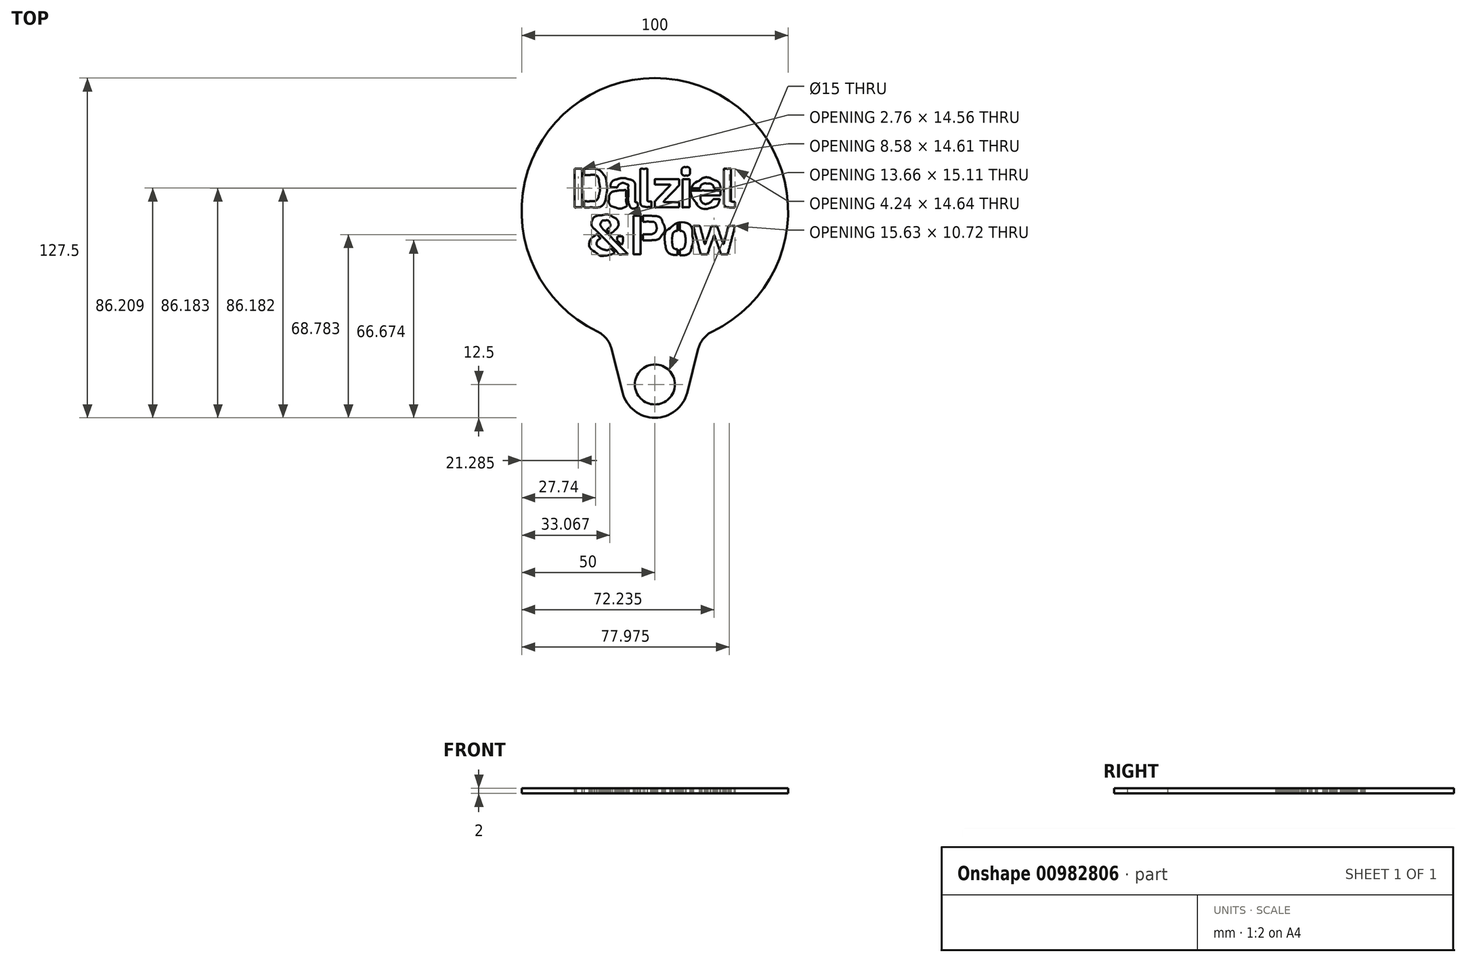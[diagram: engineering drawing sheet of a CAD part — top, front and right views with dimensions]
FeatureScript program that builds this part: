
annotation { "Feature Type Name" : "Feature", "Feature Type Description" : "" }
export const myFeature = defineFeature(function(context is Context, id is Id, definition is map)
    precondition{}
    {
        {
            var Q0;
            Q0=qCreatedBy(makeId("Top.planeOp"),FACE);
            var sketch = newSketch(context, id + "F0", { "sketchPlane" : qUnion([Q0])});
            skArc(sketch, "E0", {"start": v(21.65, -45.07) * mm, "mid": v(0, 50) * mm, "end": v(-21.65, -45.07) * mm});
            skCircle(sketch, "E1", {"center": v(0, -65) * mm, "radius": 7.5 * mm});
            skArc(sketch, "E2", {"start": v(-12.12, -68.07) * mm, "mid": v(0, -77.5) * mm, "end": v(12.12, -68.07) * mm});
            skLineSegment(sketch, "E3", {"start": v(12.12, -68.07) * mm, "end": v(16.29, -51.63) * mm});
            skLineSegment(sketch, "E4", {"start": v(-12.12, -68.07) * mm, "end": v(-16.29, -51.63) * mm});
            skPoint(sketch, "E5.visualSharp", {"position": v(17.5, -46.84) * mm});
            skArc(sketch, "E5.filletArc", {"start": v(21.65, -45.07) * mm, "mid": v(18.24, -47.75) * mm, "end": v(16.29, -51.63) * mm});
            skPoint(sketch, "E6.visualSharp", {"position": v(-17.5, -46.84) * mm});
            skArc(sketch, "E6.filletArc", {"start": v(-16.29, -51.63) * mm, "mid": v(-18.24, -47.75) * mm, "end": v(-21.65, -45.07) * mm});
            skCircle(sketch, "E7", {"center": v(0, 0) * mm, "radius": 40 * mm, "construction": true});
            skSolve(sketch);
        }
        {
            var Q0;
            Q0=makeQuery(id+"F0.imprint","IMPRINT",FACE,{"disambiguationData":[TD([[makeQuery(id+"F0.imprint","IMPRINT",EDGE,{"derivedFrom":sQuery(id+"F0.wireOp",EDGE,"E0")}),1.0]])]});
            extrude(context, id + "F1", {"entities" : qUnion([Q0]), "depth" : 2 * mm, "offsetDistance" : 25 * mm});
        }
        {
            var Q0;
            Q0=makeQuery(id+"F1.opExtrude","CAP_FACE",FACE,{"disambiguationData":[OSD([sQuery(id+"F0.wireOp",EDGE,"E0"),sQuery(id+"F0.wireOp",EDGE,"E1"),sQuery(id+"F0.wireOp",EDGE,"E2"),sQuery(id+"F0.wireOp",EDGE,"E3"),sQuery(id+"F0.wireOp",EDGE,"E4"),sQuery(id+"F0.wireOp",EDGE,"E5.filletArc"),sQuery(id+"F0.wireOp",EDGE,"E6.filletArc")])],"isStart":false});
            var sketch = newSketch(context, id + "F2", { "sketchPlane" : qUnion([Q0])});
            skFitSpline(sketch, "E8", {"points": [v(-115.22, -58.84) * mm, v(-108.7, -64.77) * mm, v(-102.51, -70.4) * mm, v(-95.99, -76.34) * mm]});
            skFitSpline(sketch, "E9", {"points": [v(-95.99, -76.34) * mm, v(-95.26, -72.37) * mm, v(-94.43, -67.86) * mm, v(-93.51, -62.86) * mm]});
            skFitSpline(sketch, "E10", {"points": [v(-93.51, -62.86) * mm, v(-89.6, -62.86) * mm, v(-85.37, -62.77) * mm, v(-81.15, -62.96) * mm, v(-80.64, -62.98) * mm, v(-79.78, -64.47) * mm, v(-79.78, -65.27) * mm]});
            skFitSpline(sketch, "E11", {"points": [v(-79.78, -65.27) * mm, v(-79.84, -72.6) * mm, v(-80.93, -79.77) * mm, v(-84.6, -86.27) * mm]});
            skFitSpline(sketch, "E12", {"points": [v(-84.6, -86.27) * mm, v(-85.64, -88.12) * mm, v(-85.45, -89.2) * mm, v(-84, -90.64) * mm, v(-78.63, -95.97) * mm, v(-73.37, -101.42) * mm, v(-67.36, -107.55) * mm]});
            skFitSpline(sketch, "E13", {"points": [v(-67.36, -107.55) * mm, v(-72.03, -107.55) * mm, v(-75.8, -107.55) * mm, v(-79.58, -107.55) * mm, v(-80.11, -107.55) * mm, v(-80.66, -107.48) * mm, v(-81.18, -107.57) * mm]});
            skFitSpline(sketch, "E14", {"points": [v(-81.18, -107.57) * mm, v(-86.67, -108.51) * mm, v(-90.92, -106.64) * mm, v(-94.07, -102.07) * mm]});
            skFitSpline(sketch, "E15", {"points": [v(-94.07, -102.07) * mm, v(-94.3, -101.73) * mm, v(-94.6, -101.45) * mm, v(-94.93, -101.15) * mm]});
            skFitSpline(sketch, "E16", {"points": [v(-94.93, -101.15) * mm, v(-95.27, -100.86) * mm, v(-95.64, -100.56) * mm, v(-96, -100.21) * mm]});
            skFitSpline(sketch, "E17", {"points": [v(-96, -100.21) * mm, v(-101.66, -104.58) * mm, v(-107.8, -107.75) * mm, v(-114.72, -109.12) * mm]});
            skFitSpline(sketch, "E18", {"points": [v(-114.72, -109.12) * mm, v(-126.83, -111.51) * mm, v(-138.43, -110.51) * mm, v(-148.52, -102.67) * mm, v(-161.86, -92.3) * mm, v(-162.73, -73.3) * mm, v(-150.49, -61.65) * mm]});
            skFitSpline(sketch, "E19", {"points": [v(-150.49, -61.65) * mm, v(-147.66, -58.96) * mm, v(-144.36, -56.75) * mm, v(-141.02, -54.12) * mm]});
            skFitSpline(sketch, "E20", {"points": [v(-141.02, -54.12) * mm, v(-142.36, -52.6) * mm, v(-143.68, -51.12) * mm, v(-145, -49.63) * mm]});
            skFitSpline(sketch, "E21", {"points": [v(-145, -49.63) * mm, v(-158.06, -34.86) * mm, v(-151.72, -14.63) * mm, v(-132.53, -10.05) * mm]});
            skFitSpline(sketch, "E22", {"points": [v(-132.53, -10.05) * mm, v(-123.34, -7.85) * mm, v(-114.4, -8.67) * mm, v(-106.25, -13.71) * mm]});
            skFitSpline(sketch, "E23", {"points": [v(-106.25, -13.71) * mm, v(-94.34, -21.08) * mm, v(-91.86, -37.55) * mm, v(-101.24, -47.98) * mm]});
            skFitSpline(sketch, "E24", {"points": [v(-101.24, -47.98) * mm, v(-104.27, -51.34) * mm, v(-108.26, -53.83) * mm, v(-111.84, -56.67) * mm]});
            skFitSpline(sketch, "E25", {"points": [v(-111.84, -56.67) * mm, v(-112.73, -57.38) * mm, v(-113.75, -57.9) * mm, v(-115.22, -58.84) * mm]});
            skFitSpline(sketch, "E26", {"points": [v(-106.68, -89.79) * mm, v(-107.44, -88.82) * mm, v(-107.9, -88.13) * mm, v(-108.47, -87.54) * mm]});
            skFitSpline(sketch, "E27", {"points": [v(-108.47, -87.54) * mm, v(-114.29, -81.44) * mm, v(-120.12, -75.35) * mm, v(-125.96, -69.28) * mm, v(-130.75, -64.32) * mm, v(-130.76, -64.33) * mm, v(-136.43, -68.46) * mm]});
            skFitSpline(sketch, "E28", {"points": [v(-136.43, -68.46) * mm, v(-143.99, -73.95) * mm, v(-145.29, -83.81) * mm, v(-138.9, -90.1) * mm]});
            skFitSpline(sketch, "E29", {"points": [v(-138.9, -90.1) * mm, v(-136.72, -92.25) * mm, v(-133.7, -94.03) * mm, v(-130.76, -94.81) * mm, v(-122.11, -97.1) * mm, v(-113.96, -95.93) * mm, v(-106.68, -89.79) * mm]});
            skFitSpline(sketch, "E30", {"points": [v(-123.71, -22.65) * mm, v(-128.16, -22.58) * mm, v(-132, -23.9) * mm, v(-134.27, -27.96) * mm]});
            skFitSpline(sketch, "E31", {"points": [v(-134.27, -27.96) * mm, v(-136.7, -32.27) * mm, v(-135.63, -36.43) * mm, v(-133, -40.28) * mm]});
            skFitSpline(sketch, "E32", {"points": [v(-133, -40.28) * mm, v(-130.2, -44.4) * mm, v(-127.93, -46.57) * mm, v(-125.44, -46.93) * mm]});
            skFitSpline(sketch, "E33", {"points": [v(-125.44, -46.93) * mm, v(-122.96, -47.29) * mm, v(-120.24, -45.83) * mm, v(-116.54, -42.67) * mm]});
            skFitSpline(sketch, "E34", {"points": [v(-116.54, -42.67) * mm, v(-112.54, -39.25) * mm, v(-111.09, -34.1) * mm, v(-112.8, -29.39) * mm]});
            skFitSpline(sketch, "E35", {"points": [v(-112.8, -29.39) * mm, v(-114.33, -25.13) * mm, v(-118.23, -22.72) * mm, v(-123.71, -22.65) * mm]});
            skFitSpline(sketch, "E36", {"points": [v(-200.46, 58.06) * mm, v(-200.46, 72.91) * mm, v(-200.4, 87.77) * mm, v(-200.52, 102.63) * mm]});
            skFitSpline(sketch, "E37", {"points": [v(-200.52, 102.63) * mm, v(-200.54, 105.52) * mm, v(-199.8, 106.47) * mm, v(-196.77, 106.43) * mm]});
            skFitSpline(sketch, "E38", {"points": [v(-196.77, 106.43) * mm, v(-184.27, 106.25) * mm, v(-171.75, 106.6) * mm, v(-159.26, 106.27) * mm]});
            skFitSpline(sketch, "E39", {"points": [v(-159.26, 106.27) * mm, v(-148.14, 105.98) * mm, v(-137.97, 102.84) * mm, v(-130.22, 94.2) * mm, v(-124.58, 87.92) * mm, v(-121.83, 80.37) * mm, v(-120.81, 72.16) * mm, v(-120.11, 66.51) * mm, v(-119.74, 60.86) * mm, v(-119.86, 55.22) * mm]});
            skFitSpline(sketch, "E40", {"points": [v(-119.86, 55.22) * mm, v(-119.98, 49.59) * mm, v(-120.6, 43.97) * mm, v(-121.87, 38.38) * mm]});
            skFitSpline(sketch, "E41", {"points": [v(-121.87, 38.38) * mm, v(-125.76, 21.35) * mm, v(-139.23, 10.19) * mm, v(-156.73, 9.85) * mm]});
            skFitSpline(sketch, "E42", {"points": [v(-156.73, 9.85) * mm, v(-170.3, 9.58) * mm, v(-183.87, 9.81) * mm, v(-197.45, 9.68) * mm]});
            skFitSpline(sketch, "E43", {"points": [v(-197.45, 9.68) * mm, v(-199.94, 9.65) * mm, v(-200.48, 10.57) * mm, v(-200.47, 12.85) * mm]});
            skFitSpline(sketch, "E44", {"points": [v(-200.47, 12.85) * mm, v(-200.4, 27.92) * mm, v(-200.43, 42.99) * mm, v(-200.43, 58.06) * mm]});
            skFitSpline(sketch, "E45", {"points": [v(-200.43, 58.06) * mm, v(-200.44, 58.06) * mm, v(-200.45, 58.06) * mm, v(-200.46, 58.06) * mm]});
            skFitSpline(sketch, "E46", {"points": [v(-182.32, 57.9) * mm, v(-182.32, 52.99) * mm, v(-182.32, 48.08) * mm, v(-182.32, 43.16) * mm, v(-182.32, 38.14) * mm, v(-182.3, 33.12) * mm, v(-182.35, 28.1) * mm]});
            skFitSpline(sketch, "E47", {"points": [v(-182.35, 28.1) * mm, v(-182.36, 26.32) * mm, v(-182.2, 24.93) * mm, v(-179.85, 24.96) * mm]});
            skFitSpline(sketch, "E48", {"points": [v(-179.85, 24.96) * mm, v(-172.91, 25.05) * mm, v(-165.95, 24.77) * mm, v(-159.03, 25.15) * mm, v(-149.46, 25.67) * mm, v(-142.81, 31.1) * mm, v(-140.32, 40.4) * mm]});
            skFitSpline(sketch, "E49", {"points": [v(-140.32, 40.4) * mm, v(-137.48, 50.97) * mm, v(-137.51, 61.79) * mm, v(-139.6, 72.44) * mm]});
            skFitSpline(sketch, "E50", {"points": [v(-139.6, 72.44) * mm, v(-142.12, 85.3) * mm, v(-149.21, 90.75) * mm, v(-162.25, 90.81) * mm]});
            skFitSpline(sketch, "E51", {"points": [v(-162.25, 90.81) * mm, v(-167.8, 90.84) * mm, v(-173.36, 90.7) * mm, v(-178.91, 90.87) * mm]});
            skFitSpline(sketch, "E52", {"points": [v(-178.91, 90.87) * mm, v(-181.6, 90.95) * mm, v(-182.4, 90.02) * mm, v(-182.37, 87.4) * mm, v(-182.25, 77.56) * mm, v(-182.32, 67.73) * mm, v(-182.32, 57.9) * mm]});
            skFitSpline(sketch, "E53", {"points": [v(96.27, -36.8) * mm, v(101.4, -36.8) * mm, v(106.4, -36.7) * mm, v(111.4, -36.9) * mm]});
            skFitSpline(sketch, "E54", {"points": [v(111.4, -36.9) * mm, v(112.1, -36.94) * mm, v(113.14, -38.32) * mm, v(113.39, -39.24) * mm]});
            skFitSpline(sketch, "E55", {"points": [v(113.39, -39.24) * mm, v(116.9, -52.55) * mm, v(120.32, -65.88) * mm, v(123.77, -79.2) * mm]});
            skFitSpline(sketch, "E56", {"points": [v(123.77, -79.2) * mm, v(124.05, -80.3) * mm, v(124.38, -81.4) * mm, v(125.38, -82.6) * mm]});
            skFitSpline(sketch, "E57", {"points": [v(125.38, -82.6) * mm, v(125.89, -81.4) * mm, v(126.48, -80.23) * mm, v(126.9, -79) * mm]});
            skFitSpline(sketch, "E58", {"points": [v(126.9, -79) * mm, v(131.27, -66.29) * mm, v(135.68, -53.59) * mm, v(139.9, -40.83) * mm]});
            skFitSpline(sketch, "E59", {"points": [v(139.9, -40.83) * mm, v(140.7, -38.4) * mm, v(141.77, -37.31) * mm, v(144.4, -37.5) * mm]});
            skFitSpline(sketch, "E60", {"points": [v(144.4, -37.5) * mm, v(147.26, -37.72) * mm, v(150.16, -37.65) * mm, v(153.04, -37.54) * mm]});
            skFitSpline(sketch, "E61", {"points": [v(153.04, -37.54) * mm, v(155.08, -37.45) * mm, v(156.02, -38.24) * mm, v(156.7, -40.2) * mm]});
            skFitSpline(sketch, "E62", {"points": [v(156.7, -40.2) * mm, v(161.05, -53.04) * mm, v(165.54, -65.82) * mm, v(170, -78.62) * mm, v(170.45, -79.9) * mm, v(170.96, -81.16) * mm, v(171.44, -82.43) * mm]});
            skFitSpline(sketch, "E63", {"points": [v(171.44, -82.43) * mm, v(171.73, -82.45) * mm, v(172.01, -82.46) * mm, v(172.3, -82.48) * mm]});
            skFitSpline(sketch, "E64", {"points": [v(172.3, -82.48) * mm, v(173.31, -78.46) * mm, v(174.33, -74.44) * mm, v(175.34, -70.4) * mm]});
            skFitSpline(sketch, "E65", {"points": [v(175.34, -70.4) * mm, v(177.88, -60.27) * mm, v(180.46, -50.14) * mm, v(182.9, -39.97) * mm]});
            skFitSpline(sketch, "E66", {"points": [v(182.9, -39.97) * mm, v(183.47, -37.64) * mm, v(184.4, -36.56) * mm, v(187, -36.7) * mm]});
            skFitSpline(sketch, "E67", {"points": [v(187, -36.7) * mm, v(191.24, -36.92) * mm, v(195.5, -36.76) * mm, v(200.35, -36.76) * mm]});
            skFitSpline(sketch, "E68", {"points": [v(200.35, -36.76) * mm, v(199.1, -41.88) * mm, v(198, -46.6) * mm, v(196.78, -51.28) * mm]});
            skFitSpline(sketch, "E69", {"points": [v(196.78, -51.28) * mm, v(192.2, -68.93) * mm, v(187.55, -86.57) * mm, v(183.05, -104.25) * mm]});
            skFitSpline(sketch, "E70", {"points": [v(183.05, -104.25) * mm, v(182.4, -106.76) * mm, v(181.37, -107.8) * mm, v(178.7, -107.6) * mm]});
            skFitSpline(sketch, "E71", {"points": [v(178.7, -107.6) * mm, v(175.52, -107.37) * mm, v(172.29, -107.4) * mm, v(169.1, -107.6) * mm]});
            skFitSpline(sketch, "E72", {"points": [v(169.1, -107.6) * mm, v(166.55, -107.76) * mm, v(165.31, -106.9) * mm, v(164.46, -104.42) * mm]});
            skFitSpline(sketch, "E73", {"points": [v(164.46, -104.42) * mm, v(159.8, -90.9) * mm, v(154.94, -77.46) * mm, v(150.14, -63.99) * mm]});
            skFitSpline(sketch, "E74", {"points": [v(150.14, -63.99) * mm, v(149.72, -62.8) * mm, v(149.2, -61.65) * mm, v(148.36, -59.55) * mm]});
            skFitSpline(sketch, "E75", {"points": [v(148.36, -59.55) * mm, v(147.61, -61.4) * mm, v(147.17, -62.38) * mm, v(146.82, -63.4) * mm, v(142, -77.09) * mm, v(137.16, -90.77) * mm, v(132.46, -104.5) * mm]});
            skFitSpline(sketch, "E76", {"points": [v(132.46, -104.5) * mm, v(131.67, -106.77) * mm, v(130.6, -107.74) * mm, v(128.13, -107.6) * mm]});
            skFitSpline(sketch, "E77", {"points": [v(128.13, -107.6) * mm, v(124.5, -107.39) * mm, v(120.85, -107.7) * mm, v(117.24, -107.44) * mm, v(116.19, -107.37) * mm, v(114.57, -106.31) * mm, v(114.32, -105.4) * mm]});
            skFitSpline(sketch, "E78", {"points": [v(114.32, -105.4) * mm, v(108.17, -82.97) * mm, v(102.18, -60.5) * mm, v(96.17, -38.03) * mm]});
            skFitSpline(sketch, "E79", {"points": [v(96.17, -38.03) * mm, v(96.12, -37.85) * mm, v(96.2, -37.62) * mm, v(96.27, -36.8) * mm]});
            skFitSpline(sketch, "E80", {"points": [v(-53.69, -10.92) * mm, v(-51.83, -10.92) * mm, v(-50.46, -10.9) * mm, v(-49.1, -10.92) * mm]});
            skFitSpline(sketch, "E81", {"points": [v(-49.1, -10.92) * mm, v(-34.57, -11.11) * mm, v(-20.01, -10.76) * mm, v(-5.54, -11.68) * mm]});
            skFitSpline(sketch, "E82", {"points": [v(-5.54, -11.68) * mm, v(5.55, -12.4) * mm, v(15.07, -17.37) * mm, v(19.71, -28.18) * mm]});
            skFitSpline(sketch, "E83", {"points": [v(19.71, -28.18) * mm, v(24.46, -39.24) * mm, v(24.01, -50.38) * mm, v(16.78, -60.45) * mm]});
            skFitSpline(sketch, "E84", {"points": [v(16.78, -60.45) * mm, v(10.77, -68.83) * mm, v(1.72, -71.82) * mm, v(-8.05, -72.47) * mm, v(-16.04, -73) * mm, v(-24.07, -72.8) * mm, v(-32.09, -72.72) * mm]});
            skFitSpline(sketch, "E85", {"points": [v(-32.09, -72.72) * mm, v(-33.4, -72.7) * mm, v(-34.29, -72.92) * mm, v(-34.83, -73.46) * mm]});
            skFitSpline(sketch, "E86", {"points": [v(-34.83, -73.46) * mm, v(-35.37, -74) * mm, v(-35.59, -74.89) * mm, v(-35.57, -76.21) * mm, v(-35.45, -85.5) * mm, v(-35.6, -94.8) * mm, v(-35.5, -104.1) * mm]});
            skFitSpline(sketch, "E87", {"points": [v(-35.5, -104.1) * mm, v(-35.46, -106.7) * mm, v(-36.17, -107.78) * mm, v(-38.9, -107.64) * mm]});
            skFitSpline(sketch, "E88", {"points": [v(-38.9, -107.64) * mm, v(-42.64, -107.46) * mm, v(-46.4, -107.45) * mm, v(-50.12, -107.66) * mm]});
            skFitSpline(sketch, "E89", {"points": [v(-50.12, -107.66) * mm, v(-52.89, -107.8) * mm, v(-53.76, -106.96) * mm, v(-53.75, -104.08) * mm]});
            skFitSpline(sketch, "E90", {"points": [v(-53.75, -104.08) * mm, v(-53.64, -75.76) * mm, v(-53.69, -47.44) * mm, v(-53.69, -19.13) * mm]});
            skFitSpline(sketch, "E91", {"points": [v(-53.69, -19.13) * mm, v(-53.69, -16.58) * mm, v(-53.69, -14.02) * mm, v(-53.69, -10.92) * mm]});
            skFitSpline(sketch, "E92", {"points": [v(-35.52, -42.1) * mm, v(-35.52, -46.38) * mm, v(-35.46, -50.65) * mm, v(-35.55, -54.91) * mm]});
            skFitSpline(sketch, "E93", {"points": [v(-35.55, -54.91) * mm, v(-35.59, -56.86) * mm, v(-35.12, -57.82) * mm, v(-32.89, -57.79) * mm]});
            skFitSpline(sketch, "E94", {"points": [v(-32.89, -57.79) * mm, v(-25.74, -57.66) * mm, v(-18.58, -57.98) * mm, v(-11.45, -57.59) * mm]});
            skFitSpline(sketch, "E95", {"points": [v(-11.45, -57.59) * mm, v(-8.38, -57.42) * mm, v(-5.1, -56.41) * mm, v(-2.4, -54.9) * mm]});
            skFitSpline(sketch, "E96", {"points": [v(-2.4, -54.9) * mm, v(0.32, -53.37) * mm, v(2.26, -50.86) * mm, v(3.33, -47.89) * mm]});
            skFitSpline(sketch, "E97", {"points": [v(3.33, -47.89) * mm, v(4.4, -44.91) * mm, v(4.6, -41.47) * mm, v(3.85, -38.06) * mm]});
            skFitSpline(sketch, "E98", {"points": [v(3.85, -38.06) * mm, v(2.4, -31.54) * mm, v(-2.28, -26.93) * mm, v(-9.32, -26.42) * mm]});
            skFitSpline(sketch, "E99", {"points": [v(-9.32, -26.42) * mm, v(-17.28, -25.83) * mm, v(-25.3, -26.07) * mm, v(-33.3, -25.93) * mm]});
            skFitSpline(sketch, "E100", {"points": [v(-33.3, -25.93) * mm, v(-35.26, -25.9) * mm, v(-35.53, -27.11) * mm, v(-35.52, -28.66) * mm, v(-35.5, -33.15) * mm, v(-35.51, -37.63) * mm, v(-35.52, -42.1) * mm]});
            skFitSpline(sketch, "E101", {"points": [v(-110.6, 59.65) * mm, v(-110.02, 69.52) * mm, v(-103.97, 77.04) * mm, v(-94.11, 80.03) * mm]});
            skFitSpline(sketch, "E102", {"points": [v(-94.11, 80.03) * mm, v(-84.93, 82.8) * mm, v(-75.58, 83) * mm, v(-66.32, 80.33) * mm]});
            skFitSpline(sketch, "E103", {"points": [v(-66.32, 80.33) * mm, v(-55.87, 77.32) * mm, v(-49.85, 69.6) * mm, v(-49.6, 58.68) * mm]});
            skFitSpline(sketch, "E104", {"points": [v(-49.6, 58.68) * mm, v(-49.38, 48.96) * mm, v(-49.5, 39.23) * mm, v(-49.47, 29.51) * mm]});
            skFitSpline(sketch, "E105", {"points": [v(-49.47, 29.51) * mm, v(-49.46, 23.34) * mm, v(-49.14, 22.94) * mm, v(-42.98, 22.06) * mm]});
            skFitSpline(sketch, "E106", {"points": [v(-42.98, 22.06) * mm, v(-42.98, 18.63) * mm, v(-42.84, 15.13) * mm, v(-43.09, 11.66) * mm]});
            skFitSpline(sketch, "E107", {"points": [v(-43.09, 11.66) * mm, v(-43.14, 10.88) * mm, v(-44.42, 9.84) * mm, v(-45.35, 9.51) * mm]});
            skFitSpline(sketch, "E108", {"points": [v(-45.35, 9.51) * mm, v(-53.8, 6.5) * mm, v(-60.49, 9.4) * mm, v(-64.11, 16.97) * mm]});
            skFitSpline(sketch, "E109", {"points": [v(-64.11, 16.97) * mm, v(-68.43, 14.49) * mm, v(-72.56, 11.4) * mm, v(-77.2, 9.6) * mm]});
            skFitSpline(sketch, "E110", {"points": [v(-77.2, 9.6) * mm, v(-84.72, 6.7) * mm, v(-92.56, 7.34) * mm, v(-100.1, 10.05) * mm]});
            skFitSpline(sketch, "E111", {"points": [v(-100.1, 10.05) * mm, v(-109.53, 13.43) * mm, v(-114.73, 21.45) * mm, v(-114.28, 31.37) * mm]});
            skFitSpline(sketch, "E112", {"points": [v(-114.28, 31.37) * mm, v(-113.85, 40.67) * mm, v(-107.4, 48.27) * mm, v(-96.96, 50.57) * mm]});
            skFitSpline(sketch, "E113", {"points": [v(-96.96, 50.57) * mm, v(-90.85, 51.91) * mm, v(-84.49, 52.07) * mm, v(-78.23, 52.7) * mm]});
            skFitSpline(sketch, "E114", {"points": [v(-78.23, 52.7) * mm, v(-75.15, 53) * mm, v(-72.06, 53.24) * mm, v(-68.97, 53.38) * mm]});
            skFitSpline(sketch, "E115", {"points": [v(-68.97, 53.38) * mm, v(-67.2, 53.45) * mm, v(-66.6, 54.2) * mm, v(-66.59, 55.95) * mm]});
            skFitSpline(sketch, "E116", {"points": [v(-66.59, 55.95) * mm, v(-66.56, 60.87) * mm, v(-66.49, 65.9) * mm, v(-71.96, 68.22) * mm]});
            skFitSpline(sketch, "E117", {"points": [v(-71.96, 68.22) * mm, v(-77.43, 70.54) * mm, v(-83.14, 70.5) * mm, v(-88.34, 67.62) * mm]});
            skFitSpline(sketch, "E118", {"points": [v(-88.34, 67.62) * mm, v(-90.37, 66.5) * mm, v(-91.88, 64.07) * mm, v(-93.08, 61.93) * mm]});
            skFitSpline(sketch, "E119", {"points": [v(-93.08, 61.93) * mm, v(-93.9, 60.47) * mm, v(-94.46, 59.57) * mm, v(-96.29, 59.61) * mm]});
            skFitSpline(sketch, "E120", {"points": [v(-96.29, 59.61) * mm, v(-101.05, 59.72) * mm, v(-105.81, 59.65) * mm, v(-110.6, 59.65) * mm]});
            skFitSpline(sketch, "E121", {"points": [v(-66.65, 35.75) * mm, v(-66.53, 41.33) * mm, v(-66.53, 41.3) * mm, v(-70.84, 40.92) * mm, v(-72.64, 40.76) * mm, v(-74.47, 40.86) * mm, v(-76.27, 40.64) * mm]});
            skFitSpline(sketch, "E122", {"points": [v(-76.27, 40.64) * mm, v(-81.2, 40.05) * mm, v(-86.24, 39.77) * mm, v(-91.04, 38.56) * mm, v(-93.06, 38.05) * mm, v(-94.63, 36.85) * mm, v(-95.69, 35.33) * mm]});
            skFitSpline(sketch, "E123", {"points": [v(-95.69, 35.33) * mm, v(-96.74, 33.8) * mm, v(-97.28, 31.96) * mm, v(-97.23, 30.17) * mm]});
            skFitSpline(sketch, "E124", {"points": [v(-97.23, 30.17) * mm, v(-97.12, 26.44) * mm, v(-94.43, 23.13) * mm, v(-90.36, 21.86) * mm]});
            skFitSpline(sketch, "E125", {"points": [v(-90.36, 21.86) * mm, v(-85.42, 20.32) * mm, v(-80.62, 21.24) * mm, v(-76.04, 23.16) * mm]});
            skFitSpline(sketch, "E126", {"points": [v(-76.04, 23.16) * mm, v(-69.94, 25.72) * mm, v(-66.94, 30.56) * mm, v(-66.65, 35.75) * mm]});
            skFitSpline(sketch, "E127", {"points": [v(164.3, 40) * mm, v(159.84, 40) * mm, v(156, 40) * mm, v(152.18, 40) * mm]});
            skFitSpline(sketch, "E128", {"points": [v(152.18, 40) * mm, v(140.53, 40) * mm, v(128.88, 40.01) * mm, v(117.23, 40) * mm]});
            skFitSpline(sketch, "E129", {"points": [v(117.23, 40) * mm, v(113.68, 40) * mm, v(113.33, 39.56) * mm, v(113.92, 36.1) * mm]});
            skFitSpline(sketch, "E130", {"points": [v(113.92, 36.1) * mm, v(115.91, 24.55) * mm, v(126.74, 17.96) * mm, v(137.66, 22.16) * mm]});
            skFitSpline(sketch, "E131", {"points": [v(137.66, 22.16) * mm, v(140.39, 23.2) * mm, v(142.36, 26.2) * mm, v(144.69, 28.28) * mm, v(145.49, 29) * mm, v(146.3, 30.23) * mm, v(147.14, 30.26) * mm]});
            skFitSpline(sketch, "E132", {"points": [v(147.14, 30.26) * mm, v(152.03, 30.45) * mm, v(156.93, 30.35) * mm, v(162.33, 30.35) * mm]});
            skFitSpline(sketch, "E133", {"points": [v(162.33, 30.35) * mm, v(161.97, 28.75) * mm, v(161.84, 27.52) * mm, v(161.4, 26.42) * mm]});
            skFitSpline(sketch, "E134", {"points": [v(161.4, 26.42) * mm, v(157.5, 16.56) * mm, v(150.09, 11) * mm, v(139.86, 8.75) * mm]});
            skFitSpline(sketch, "E135", {"points": [v(139.86, 8.75) * mm, v(124.59, 5.4) * mm, v(110.22, 10.65) * mm, v(102, 22.75) * mm, v(90.89, 39.14) * mm, v(94.82, 65.68) * mm, v(110.38, 76.16) * mm]});
            skFitSpline(sketch, "E136", {"points": [v(110.38, 76.16) * mm, v(121.95, 83.95) * mm, v(134.65, 84.3) * mm, v(147, 78.37) * mm]});
            skFitSpline(sketch, "E137", {"points": [v(147, 78.37) * mm, v(158.8, 72.7) * mm, v(163.78, 62.2) * mm, v(164.28, 49.42) * mm]});
            skFitSpline(sketch, "E138", {"points": [v(164.28, 49.42) * mm, v(164.4, 46.46) * mm, v(164.3, 43.48) * mm, v(164.3, 40) * mm]});
            skFitSpline(sketch, "E139", {"points": [v(146.4, 51.95) * mm, v(146.81, 61.72) * mm, v(141.05, 68.35) * mm, v(132.19, 68.91) * mm]});
            skFitSpline(sketch, "E140", {"points": [v(132.19, 68.91) * mm, v(122.38, 69.53) * mm, v(114.57, 63.44) * mm, v(113.7, 54.59) * mm]});
            skFitSpline(sketch, "E141", {"points": [v(113.7, 54.59) * mm, v(113.6, 53.6) * mm, v(113.71, 52.93) * mm, v(114.1, 52.5) * mm]});
            skFitSpline(sketch, "E142", {"points": [v(114.1, 52.5) * mm, v(114.49, 52.08) * mm, v(115.15, 51.9) * mm, v(116.14, 51.93) * mm]});
            skFitSpline(sketch, "E143", {"points": [v(116.14, 51.93) * mm, v(120.2, 52.02) * mm, v(124.26, 51.95) * mm, v(128.33, 51.95) * mm]});
            skFitSpline(sketch, "E144", {"points": [v(128.33, 51.95) * mm, v(134.29, 51.95) * mm, v(140.25, 51.95) * mm, v(146.4, 51.95) * mm]});
            skFitSpline(sketch, "E145", {"points": [v(24.46, -72.26) * mm, v(24.69, -60.05) * mm, v(28.1, -49.32) * mm, v(38.3, -41.88) * mm, v(56.4, -28.65) * mm, v(88.12, -34.4) * mm, v(93.87, -62) * mm]});
            skFitSpline(sketch, "E146", {"points": [v(93.87, -62) * mm, v(95.66, -70.6) * mm, v(95.46, -79.22) * mm, v(92.44, -87.56) * mm]});
            skFitSpline(sketch, "E147", {"points": [v(92.44, -87.56) * mm, v(86.2, -104.83) * mm, v(70.04, -110.5) * mm, v(56.63, -109.31) * mm]});
            skFitSpline(sketch, "E148", {"points": [v(56.63, -109.31) * mm, v(40.96, -107.93) * mm, v(30, -98.87) * mm, v(26.25, -84.56) * mm]});
            skFitSpline(sketch, "E149", {"points": [v(26.25, -84.56) * mm, v(25.2, -80.58) * mm, v(25.03, -76.36) * mm, v(24.46, -72.26) * mm]});
            skFitSpline(sketch, "E150", {"points": [v(42.57, -72.15) * mm, v(42.91, -75.25) * mm, v(43.03, -78.47) * mm, v(43.66, -81.59) * mm]});
            skFitSpline(sketch, "E151", {"points": [v(43.66, -81.59) * mm, v(45.28, -89.66) * mm, v(51.4, -94.77) * mm, v(59.36, -95.02) * mm]});
            skFitSpline(sketch, "E152", {"points": [v(59.36, -95.02) * mm, v(67.24, -95.27) * mm, v(73.69, -90.4) * mm, v(75.73, -82.44) * mm]});
            skFitSpline(sketch, "E153", {"points": [v(75.73, -82.44) * mm, v(76.57, -79.18) * mm, v(77, -75.9) * mm, v(77.03, -72.63) * mm]});
            skFitSpline(sketch, "E154", {"points": [v(77.03, -72.63) * mm, v(77.06, -69.35) * mm, v(76.68, -66.07) * mm, v(75.89, -62.8) * mm]});
            skFitSpline(sketch, "E155", {"points": [v(75.89, -62.8) * mm, v(73.82, -54.27) * mm, v(67.61, -49.31) * mm, v(59.44, -49.5) * mm]});
            skFitSpline(sketch, "E156", {"points": [v(59.44, -49.5) * mm, v(51.22, -49.68) * mm, v(45.2, -54.9) * mm, v(43.59, -63.48) * mm, v(43.06, -66.3) * mm, v(42.9, -69.18) * mm, v(42.57, -72.15) * mm]});
            skFitSpline(sketch, "E157", {"points": [v(38.72, 66.86) * mm, v(37.5, 66.86) * mm, v(36.26, 66.86) * mm, v(35.03, 66.86) * mm]});
            skFitSpline(sketch, "E158", {"points": [v(35.03, 66.86) * mm, v(24.67, 66.85) * mm, v(14.3, 67) * mm, v(3.94, 66.77) * mm]});
            skFitSpline(sketch, "E159", {"points": [v(3.94, 66.77) * mm, v(0.54, 66.69) * mm, v(-0.36, 67.84) * mm, v(-0.06, 70.95) * mm]});
            skFitSpline(sketch, "E160", {"points": [v(-0.06, 70.95) * mm, v(0.16, 73.17) * mm, v(0.06, 75.44) * mm, v(-0.03, 77.68) * mm]});
            skFitSpline(sketch, "E161", {"points": [v(-0.03, 77.68) * mm, v(-0.11, 79.57) * mm, v(0.56, 80.32) * mm, v(2.54, 80.32) * mm, v(20.92, 80.26) * mm, v(39.3, 80.26) * mm, v(57.67, 80.32) * mm]});
            skFitSpline(sketch, "E162", {"points": [v(57.67, 80.32) * mm, v(59.8, 80.33) * mm, v(60.35, 79.53) * mm, v(60.42, 77.51) * mm]});
            skFitSpline(sketch, "E163", {"points": [v(60.42, 77.51) * mm, v(60.85, 65.66) * mm, v(60.91, 65.65) * mm, v(52.76, 57.02) * mm]});
            skFitSpline(sketch, "E164", {"points": [v(52.76, 57.02) * mm, v(43.15, 46.85) * mm, v(33.5, 36.71) * mm, v(23.87, 26.56) * mm, v(23.08, 25.72) * mm, v(22.32, 24.86) * mm, v(21.74, 23.16) * mm]});
            skFitSpline(sketch, "E165", {"points": [v(21.74, 23.16) * mm, v(28.16, 23.16) * mm, v(34.59, 23.16) * mm, v(41.01, 23.16) * mm, v(47.5, 23.16) * mm, v(54, 23.16) * mm, v(60.68, 23.16) * mm]});
            skFitSpline(sketch, "E166", {"points": [v(60.68, 23.16) * mm, v(60.68, 18.65) * mm, v(60.68, 14.52) * mm, v(60.68, 10) * mm]});
            skFitSpline(sketch, "E167", {"points": [v(60.68, 10) * mm, v(59.73, 9.91) * mm, v(58.72, 9.75) * mm, v(57.7, 9.75) * mm, v(39.54, 9.73) * mm, v(21.38, 9.78) * mm, v(3.22, 9.68) * mm]});
            skFitSpline(sketch, "E168", {"points": [v(3.22, 9.68) * mm, v(0.52, 9.67) * mm, v(-0.22, 10.58) * mm, v(-0.26, 13.17) * mm, v(-0.43, 24.02) * mm, v(-0.53, 24.04) * mm, v(6.92, 31.95) * mm]});
            skFitSpline(sketch, "E169", {"points": [v(6.92, 31.95) * mm, v(16.82, 42.44) * mm, v(26.76, 52.88) * mm, v(36.68, 63.35) * mm]});
            skFitSpline(sketch, "E170", {"points": [v(36.68, 63.35) * mm, v(37.48, 64.2) * mm, v(38.24, 65.06) * mm, v(39.01, 65.92) * mm]});
            skFitSpline(sketch, "E171", {"points": [v(39.01, 65.92) * mm, v(38.92, 66.23) * mm, v(38.82, 66.54) * mm, v(38.72, 66.86) * mm]});
            skFitSpline(sketch, "E172", {"points": [v(200.5, 23.13) * mm, v(200.5, 19.12) * mm, v(200.64, 15.28) * mm, v(200.38, 11.47) * mm]});
            skFitSpline(sketch, "E173", {"points": [v(200.38, 11.47) * mm, v(200.32, 10.66) * mm, v(198.8, 9.31) * mm, v(197.96, 9.31) * mm]});
            skFitSpline(sketch, "E174", {"points": [v(197.96, 9.31) * mm, v(193.4, 9.32) * mm, v(188.71, 9.1) * mm, v(184.3, 10.05) * mm]});
            skFitSpline(sketch, "E175", {"points": [v(184.3, 10.05) * mm, v(177.06, 11.62) * mm, v(172.73, 17.72) * mm, v(172.63, 25.7) * mm]});
            skFitSpline(sketch, "E176", {"points": [v(172.63, 25.7) * mm, v(172.48, 37.77) * mm, v(172.56, 49.84) * mm, v(172.55, 61.9) * mm]});
            skFitSpline(sketch, "E177", {"points": [v(172.55, 61.9) * mm, v(172.55, 68.74) * mm, v(172.56, 75.57) * mm, v(172.56, 82.4) * mm]});
            skFitSpline(sketch, "E178", {"points": [v(172.56, 82.4) * mm, v(172.57, 89.24) * mm, v(172.56, 96.08) * mm, v(172.5, 102.91) * mm]});
            skFitSpline(sketch, "E179", {"points": [v(172.5, 102.91) * mm, v(172.49, 105.52) * mm, v(173.22, 106.55) * mm, v(175.93, 106.4) * mm]});
            skFitSpline(sketch, "E180", {"points": [v(175.93, 106.4) * mm, v(179.55, 106.2) * mm, v(183.2, 106.18) * mm, v(186.82, 106.4) * mm]});
            skFitSpline(sketch, "E181", {"points": [v(186.82, 106.4) * mm, v(189.7, 106.59) * mm, v(190.4, 105.5) * mm, v(190.39, 102.74) * mm]});
            skFitSpline(sketch, "E182", {"points": [v(190.39, 102.74) * mm, v(190.28, 80) * mm, v(190.32, 57.25) * mm, v(190.33, 34.5) * mm]});
            skFitSpline(sketch, "E183", {"points": [v(190.33, 34.5) * mm, v(190.33, 24.4) * mm, v(190.34, 24.4) * mm, v(200.5, 23.13) * mm]});
            skFitSpline(sketch, "E184", {"points": [v(-8.46, 24.27) * mm, v(-8.46, 20.28) * mm, v(-8.36, 16.34) * mm, v(-8.56, 12.42) * mm]});
            skFitSpline(sketch, "E185", {"points": [v(-8.56, 12.42) * mm, v(-8.6, 11.76) * mm, v(-9.9, 10.61) * mm, v(-10.61, 10.62) * mm]});
            skFitSpline(sketch, "E186", {"points": [v(-10.61, 10.62) * mm, v(-15.48, 10.7) * mm, v(-20.48, 10.41) * mm, v(-25.18, 11.42) * mm]});
            skFitSpline(sketch, "E187", {"points": [v(-25.18, 11.42) * mm, v(-31.58, 12.8) * mm, v(-35.85, 18.55) * mm, v(-36.35, 25.15) * mm, v(-36.63, 28.87) * mm, v(-36.6, 32.62) * mm, v(-36.6, 36.36) * mm, v(-36.63, 58.38) * mm, v(-36.56, 80.4) * mm, v(-36.68, 102.42) * mm]});
            skFitSpline(sketch, "E188", {"points": [v(-36.68, 102.42) * mm, v(-36.68, 103.94) * mm, v(-36.49, 105) * mm, v(-35.9, 105.64) * mm]});
            skFitSpline(sketch, "E189", {"points": [v(-35.9, 105.64) * mm, v(-35.3, 106.3) * mm, v(-34.32, 106.53) * mm, v(-32.74, 106.41) * mm, v(-29.34, 106.16) * mm, v(-25.89, 106.16) * mm, v(-22.48, 106.41) * mm, v(-19.6, 106.62) * mm, v(-18.85, 105.54) * mm, v(-18.86, 102.78) * mm]});
            skFitSpline(sketch, "E190", {"points": [v(-18.86, 102.78) * mm, v(-18.96, 85.25) * mm, v(-18.92, 67.72) * mm, v(-18.92, 50.2) * mm]});
            skFitSpline(sketch, "E191", {"points": [v(-18.92, 50.2) * mm, v(-18.92, 44.63) * mm, v(-18.95, 39.08) * mm, v(-18.9, 33.52) * mm, v(-18.85, 26.39) * mm, v(-17.64, 25.13) * mm, v(-10.63, 24.65) * mm]});
            skFitSpline(sketch, "E192", {"points": [v(-10.63, 24.65) * mm, v(-10, 24.6) * mm, v(-9.4, 24.44) * mm, v(-8.46, 24.27) * mm]});
            skFitSpline(sketch, "E193", {"points": [v(86.73, 9.74) * mm, v(81.2, 9.74) * mm, v(76.18, 9.8) * mm, v(71.17, 9.72) * mm]});
            skFitSpline(sketch, "E194", {"points": [v(71.17, 9.72) * mm, v(68.9, 9.68) * mm, v(68.92, 11.1) * mm, v(68.92, 12.68) * mm]});
            skFitSpline(sketch, "E195", {"points": [v(68.92, 12.68) * mm, v(68.93, 22.09) * mm, v(68.91, 31.5) * mm, v(68.91, 40.9) * mm]});
            skFitSpline(sketch, "E196", {"points": [v(68.91, 40.9) * mm, v(68.91, 46.78) * mm, v(68.91, 52.66) * mm, v(68.91, 58.54) * mm]});
            skFitSpline(sketch, "E197", {"points": [v(68.91, 58.54) * mm, v(68.91, 64.42) * mm, v(68.92, 70.3) * mm, v(68.93, 76.18) * mm]});
            skFitSpline(sketch, "E198", {"points": [v(68.93, 76.18) * mm, v(68.93, 77.44) * mm, v(69.07, 78.69) * mm, v(69.15, 80.1) * mm]});
            skFitSpline(sketch, "E199", {"points": [v(69.15, 80.1) * mm, v(75.15, 80.1) * mm, v(80.87, 80.1) * mm, v(86.73, 80.1) * mm]});
            skFitSpline(sketch, "E200", {"points": [v(86.73, 80.1) * mm, v(86.73, 56.65) * mm, v(86.73, 33.4) * mm, v(86.73, 9.74) * mm]});
            skFitSpline(sketch, "E201", {"points": [v(87.87, 100) * mm, v(87.9, 94.13) * mm, v(83.5, 89.6) * mm, v(77.68, 89.5) * mm]});
            skFitSpline(sketch, "E202", {"points": [v(77.68, 89.5) * mm, v(72.12, 89.43) * mm, v(67.24, 94.19) * mm, v(67.12, 99.82) * mm]});
            skFitSpline(sketch, "E203", {"points": [v(67.12, 99.82) * mm, v(67, 105.36) * mm, v(71.83, 110.22) * mm, v(77.5, 110.26) * mm]});
            skFitSpline(sketch, "E204", {"points": [v(77.5, 110.26) * mm, v(83.35, 110.31) * mm, v(87.83, 105.88) * mm, v(87.87, 100) * mm]});
            skSolve(sketch);
        }
        {
            var Q0;
            Q0=makeQuery(id+"F2.imprint","IMPRINT",FACE,{"disambiguationData":[TD([[makeQuery(id+"F2.imprint","IMPRINT",EDGE,{"derivedFrom":sQuery(id+"F2.wireOp",EDGE,"E36")}),-1.0]])]});
            var Q1;
            Q1=makeQuery(id+"F2.imprint","IMPRINT",FACE,{"disambiguationData":[TD([[makeQuery(id+"F2.imprint","IMPRINT",EDGE,{"derivedFrom":sQuery(id+"F2.wireOp",EDGE,"E101")}),-1.0]])]});
            var Q2;
            {var subQ1=sQuery(id+"F2.wireOp",EDGE,"E188");Q2=makeQuery(id+"F2.imprint","IMPRINT",FACE,{"disambiguationData":[TD([[makeQuery(id+"F2.imprint","IMPRINT",EDGE,{"derivedFrom":subQ1}),-1.0]])]});}
            var Q3;
            Q3=makeQuery(id+"F2.imprint","IMPRINT",FACE,{"disambiguationData":[TD([[makeQuery(id+"F2.imprint","IMPRINT",EDGE,{"derivedFrom":sQuery(id+"F2.wireOp",EDGE,"E157")}),-1.0]])]});
            var Q4;
            Q4=makeQuery(id+"F2.imprint","IMPRINT",FACE,{"disambiguationData":[TD([[makeQuery(id+"F2.imprint","IMPRINT",EDGE,{"derivedFrom":sQuery(id+"F2.wireOp",EDGE,"E201")}),-1.0]])]});
            var Q5;
            {var subQ0=sQuery(id+"F2.wireOp",EDGE,"E166");Q5=makeQuery(id+"F2.imprint","IMPRINT",FACE,{"disambiguationData":[TD([[makeQuery(id+"F2.imprint","IMPRINT",EDGE,{"derivedFrom":subQ0}),-1.0]])]});}
            var Q6;
            {var subQ0=sQuery(id+"F2.wireOp",EDGE,"E168");Q6=makeQuery(id+"F2.imprint","IMPRINT",FACE,{"disambiguationData":[TD([[makeQuery(id+"F2.imprint","IMPRINT",EDGE,{"derivedFrom":subQ0}),-1.0]])]});}
            var Q7;
            Q7=makeQuery(id+"F2.imprint","IMPRINT",FACE,{"disambiguationData":[TD([[makeQuery(id+"F2.imprint","IMPRINT",EDGE,{"derivedFrom":sQuery(id+"F2.wireOp",EDGE,"E184")}),-1.0]])]});
            var Q8;
            Q8=makeQuery(id+"F2.imprint","IMPRINT",FACE,{"disambiguationData":[TD([[makeQuery(id+"F2.imprint","IMPRINT",EDGE,{"derivedFrom":sQuery(id+"F2.wireOp",EDGE,"E193")}),-1.0]])]});
            var Q9;
            Q9=makeQuery(id+"F2.imprint","IMPRINT",FACE,{"disambiguationData":[TD([[makeQuery(id+"F2.imprint","IMPRINT",EDGE,{"derivedFrom":sQuery(id+"F2.wireOp",EDGE,"E127")}),-1.0]])]});
            var Q10;
            Q10=makeQuery(id+"F2.imprint","IMPRINT",FACE,{"disambiguationData":[TD([[makeQuery(id+"F2.imprint","IMPRINT",EDGE,{"derivedFrom":sQuery(id+"F2.wireOp",EDGE,"E172")}),-1.0]])]});
            var Q11;
            Q11=makeQuery(id+"F2.imprint","IMPRINT",FACE,{"disambiguationData":[TD([[makeQuery(id+"F2.imprint","IMPRINT",EDGE,{"derivedFrom":sQuery(id+"F2.wireOp",EDGE,"E53")}),-1.0]])]});
            var Q12;
            Q12=makeQuery(id+"F2.imprint","IMPRINT",FACE,{"disambiguationData":[TD([[makeQuery(id+"F2.imprint","IMPRINT",EDGE,{"derivedFrom":sQuery(id+"F2.wireOp",EDGE,"E145")}),-1.0]])]});
            var Q13;
            {var subQ5=sQuery(id+"F2.wireOp",EDGE,"E80");Q13=makeQuery(id+"F2.imprint","IMPRINT",FACE,{"disambiguationData":[TD([[makeQuery(id+"F2.imprint","IMPRINT",EDGE,{"derivedFrom":subQ5}),-1.0]])]});}
            var Q14;
            Q14=makeQuery(id+"F2.imprint","IMPRINT",FACE,{"disambiguationData":[TD([[makeQuery(id+"F2.imprint","IMPRINT",EDGE,{"derivedFrom":sQuery(id+"F2.wireOp",EDGE,"E8")}),-1.0]])]});
            var Q15;
            {var subQ10=sQuery(id+"F2.wireOp",EDGE,"E82");Q15=makeQuery(id+"F2.imprint","IMPRINT",FACE,{"disambiguationData":[TD([[makeQuery(id+"F2.imprint","IMPRINT",EDGE,{"derivedFrom":subQ10}),-1.0]])]});}
            var Q16;
            {var subQ0=sQuery(id+"F2.wireOp",EDGE,"E84");var subQ1=makeQuery(id+"F1.opExtrude","CAP_EDGE",EDGE,{"disambiguationData":[OSD([sQuery(id+"F0.wireOp",EDGE,"E1")])],"isStart":false});var subQ2=makeQuery(id+"F2.imprint","INTERSECT",VERTEX,{"disambiguationData":[OD(0.0)],"derivedFrom":[subQ1,subQ0]});Q16=makeQuery(id+"F2.imprint","IMPRINT",FACE,{"disambiguationData":[TD([[makeQuery(id+"F2.imprint","IMPRINT",EDGE,{"disambiguationData":[TD([[subQ2,-1.0]])],"derivedFrom":subQ0}),-1.0]])]});}
            var Q17;
            {var subQ0=makeQuery(id+"F1.opExtrude","CAP_EDGE",EDGE,{"disambiguationData":[OSD([sQuery(id+"F0.wireOp",EDGE,"E5.filletArc")])],"isStart":false});Q17=makeQuery(id+"F2.imprint","IMPRINT",FACE,{"disambiguationData":[TD([[makeQuery(id+"F2.imprint","IMPRINT",EDGE,{"derivedFrom":subQ0}),1.0]])]});}
            var Q18;
            {var subQ6=sQuery(id+"F2.wireOp",EDGE,"E106");Q18=makeQuery(id+"F2.imprint","IMPRINT",FACE,{"disambiguationData":[TD([[makeQuery(id+"F2.imprint","IMPRINT",EDGE,{"derivedFrom":subQ6}),-1.0]])]});}
            var Q19;
            Q19=sQuery(id+"F2.wireOp",EDGE,"E164");
            var Q20;
            Q20=sQuery(id+"F2.wireOp",EDGE,"E84");
            var Q21;
            Q21=sQuery(id+"F2.wireOp",EDGE,"E36");
            var Q22;
            Q22=sQuery(id+"F2.wireOp",EDGE,"E44");
            var Q23;
            Q23=sQuery(id+"F2.wireOp",EDGE,"E156");
            var Q24;
            Q24=sQuery(id+"F2.wireOp",EDGE,"E169");
            var Q25;
            Q25=sQuery(id+"F2.wireOp",EDGE,"E147");
            var Q26;
            Q26=sQuery(id+"F2.wireOp",EDGE,"E69");
            var Q27;
            Q27=sQuery(id+"F2.wireOp",EDGE,"E165");
            var Q28;
            Q28=sQuery(id+"F2.wireOp",EDGE,"E200");
            var Q29;
            Q29=sQuery(id+"F2.wireOp",EDGE,"E190");
            var Q30;
            Q30=sQuery(id+"F2.wireOp",EDGE,"E148");
            var Q31;
            Q31=sQuery(id+"F2.wireOp",EDGE,"E48");
            var Q32;
            Q32=sQuery(id+"F2.wireOp",EDGE,"E21");
            var Q33;
            Q33=sQuery(id+"F2.wireOp",EDGE,"E38");
            var Q34;
            Q34=sQuery(id+"F2.wireOp",EDGE,"E182");
            var Q35;
            Q35=sQuery(id+"F2.wireOp",EDGE,"E73");
            var Q36;
            Q36=sQuery(id+"F2.wireOp",EDGE,"E41");
            var Q37;
            Q37=sQuery(id+"F2.wireOp",EDGE,"E18");
            var Q38;
            Q38=sQuery(id+"F2.wireOp",EDGE,"E81");
            var Q39;
            Q39=sQuery(id+"F2.wireOp",EDGE,"E145");
            var Q40;
            Q40=sQuery(id+"F2.wireOp",EDGE,"E58");
            var Q41;
            Q41=sQuery(id+"F2.wireOp",EDGE,"E42");
            var Q42;
            Q42=sQuery(id+"F2.wireOp",EDGE,"E90");
            var Q43;
            Q43=sQuery(id+"F2.wireOp",EDGE,"E75");
            var Q44;
            Q44=sQuery(id+"F2.wireOp",EDGE,"E55");
            var Q45;
            Q45=sQuery(id+"F2.wireOp",EDGE,"E39");
            var Q46;
            Q46=sQuery(id+"F2.wireOp",EDGE,"E135");
            var Q47;
            Q47=sQuery(id+"F2.wireOp",EDGE,"E187");
            var Q48;
            Q48=sQuery(id+"F2.wireOp",EDGE,"E167");
            var Q49;
            Q49=sQuery(id+"F2.wireOp",EDGE,"E95");
            var Q50;
            Q50=sQuery(id+"F2.wireOp",EDGE,"E40");
            var Q51;
            Q51=sQuery(id+"F2.wireOp",EDGE,"E195");
            var Q52;
            Q52=sQuery(id+"F2.wireOp",EDGE,"E111");
            var Q53;
            Q53=sQuery(id+"F2.wireOp",EDGE,"E100");
            var Q54;
            Q54=sQuery(id+"F2.wireOp",EDGE,"E28");
            var Q55;
            Q55=sQuery(id+"F2.wireOp",EDGE,"E149");
            var Q56;
            Q56=sQuery(id+"F2.wireOp",EDGE,"E47");
            var Q57;
            Q57=sQuery(id+"F2.wireOp",EDGE,"E52");
            var Q58;
            Q58=sQuery(id+"F2.wireOp",EDGE,"E163");
            var Q59;
            Q59=sQuery(id+"F2.wireOp",EDGE,"E99");
            var Q60;
            Q60=sQuery(id+"F2.wireOp",EDGE,"E37");
            var Q61;
            Q61=sQuery(id+"F2.wireOp",EDGE,"E51");
            var Q62;
            Q62=sQuery(id+"F2.wireOp",EDGE,"E191");
            var Q63;
            Q63=sQuery(id+"F2.wireOp",EDGE,"E88");
            var Q64;
            Q64=sQuery(id+"F2.wireOp",EDGE,"E181");
            var Q65;
            Q65=sQuery(id+"F2.wireOp",EDGE,"E158");
            var Q66;
            Q66=sQuery(id+"F2.wireOp",EDGE,"E197");
            var Q67;
            Q67=sQuery(id+"F2.wireOp",EDGE,"E140");
            var Q68;
            Q68=sQuery(id+"F2.wireOp",EDGE,"E124");
            var Q69;
            Q69=sQuery(id+"F2.wireOp",EDGE,"E110");
            var Q70;
            Q70=sQuery(id+"F2.wireOp",EDGE,"E152");
            var Q71;
            Q71=sQuery(id+"F2.wireOp",EDGE,"E83");
            var Q72;
            Q72=sQuery(id+"F2.wireOp",EDGE,"E104");
            var Q73;
            Q73=sQuery(id+"F2.wireOp",EDGE,"E136");
            var Q74;
            Q74=sQuery(id+"F2.wireOp",EDGE,"E204");
            var Q75;
            Q75=sQuery(id+"F2.wireOp",EDGE,"E62");
            var Q76;
            Q76=sQuery(id+"F2.wireOp",EDGE,"E78");
            var Q77;
            Q77=sQuery(id+"F2.wireOp",EDGE,"E94");
            var Q78;
            Q78=sQuery(id+"F2.wireOp",EDGE,"E101");
            var Q79;
            Q79=sQuery(id+"F2.wireOp",EDGE,"E175");
            var Q80;
            Q80=sQuery(id+"F2.wireOp",EDGE,"E23");
            var Q81;
            Q81=sQuery(id+"F2.wireOp",EDGE,"E196");
            var Q82;
            Q82=sQuery(id+"F2.wireOp",EDGE,"E112");
            var Q83;
            Q83=sQuery(id+"F2.wireOp",EDGE,"E22");
            var Q84;
            Q84=sQuery(id+"F2.wireOp",EDGE,"E96");
            var Q85;
            Q85=sQuery(id+"F2.wireOp",EDGE,"E176");
            var Q86;
            Q86=sQuery(id+"F2.wireOp",EDGE,"E8");
            var Q87;
            Q87=sQuery(id+"F2.wireOp",EDGE,"E77");
            var Q88;
            Q88=sQuery(id+"F2.wireOp",EDGE,"E29");
            var Q89;
            Q89=sQuery(id+"F2.wireOp",EDGE,"E134");
            var Q90;
            Q90=sQuery(id+"F2.wireOp",EDGE,"E86");
            var Q91;
            Q91=sQuery(id+"F2.wireOp",EDGE,"E11");
            var Q92;
            Q92=sQuery(id+"F2.wireOp",EDGE,"E189");
            var Q93;
            Q93=sQuery(id+"F2.wireOp",EDGE,"E157");
            var Q94;
            Q94=sQuery(id+"F2.wireOp",EDGE,"E150");
            var Q95;
            Q95=sQuery(id+"F2.wireOp",EDGE,"E137");
            var Q96;
            Q96=sQuery(id+"F2.wireOp",EDGE,"E89");
            var Q97;
            Q97=sQuery(id+"F2.wireOp",EDGE,"E17");
            var Q98;
            Q98=sQuery(id+"F2.wireOp",EDGE,"E19");
            var Q99;
            Q99=sQuery(id+"F2.wireOp",EDGE,"E49");
            var Q100;
            Q100=sQuery(id+"F2.wireOp",EDGE,"E97");
            var Q101;
            Q101=sQuery(id+"F2.wireOp",EDGE,"E65");
            var Q102;
            Q102=sQuery(id+"F2.wireOp",EDGE,"E177");
            var Q103;
            Q103=sQuery(id+"F2.wireOp",EDGE,"E161");
            var Q104;
            Q104=sQuery(id+"F2.wireOp",EDGE,"E193");
            var Q105;
            Q105=sQuery(id+"F2.wireOp",EDGE,"E74");
            var Q106;
            Q106=sQuery(id+"F2.wireOp",EDGE,"E170");
            var Q107;
            Q107=sQuery(id+"F2.wireOp",EDGE,"E50");
            var Q108;
            Q108=sQuery(id+"F2.wireOp",EDGE,"E98");
            var Q109;
            Q109=sQuery(id+"F2.wireOp",EDGE,"E82");
            var Q110;
            Q110=sQuery(id+"F2.wireOp",EDGE,"E178");
            var Q111;
            Q111=sQuery(id+"F2.wireOp",EDGE,"E146");
            var Q112;
            Q112=sQuery(id+"F2.wireOp",EDGE,"E130");
            var Q113;
            Q113=sQuery(id+"F2.wireOp",EDGE,"E46");
            var Q114;
            Q114=sQuery(id+"F2.wireOp",EDGE,"E59");
            var Q115;
            Q115=sQuery(id+"F2.wireOp",EDGE,"E43");
            var Q116;
            Q116=sQuery(id+"F2.wireOp",EDGE,"E27");
            var Q117;
            Q117=sQuery(id+"F2.wireOp",EDGE,"E139");
            var Q118;
            Q118=sQuery(id+"F2.wireOp",EDGE,"E123");
            var Q119;
            Q119=sQuery(id+"F2.wireOp",EDGE,"E103");
            var Q120;
            Q120=sQuery(id+"F2.wireOp",EDGE,"E87");
            var Q121;
            Q121=sQuery(id+"F2.wireOp",EDGE,"E203");
            var Q122;
            Q122=sQuery(id+"F2.wireOp",EDGE,"E183");
            var Q123;
            Q123=sQuery(id+"F2.wireOp",EDGE,"E171");
            var Q124;
            Q124=sQuery(id+"F2.wireOp",EDGE,"E151");
            var Q125;
            Q125=sQuery(id+"F2.wireOp",EDGE,"E155");
            var Q126;
            Q126=sQuery(id+"F2.wireOp",EDGE,"E72");
            var Q127;
            Q127=sQuery(id+"F2.wireOp",EDGE,"E68");
            var Q128;
            Q128=sQuery(id+"F2.wireOp",EDGE,"E180");
            var Q129;
            Q129=sQuery(id+"F2.wireOp",EDGE,"E31");
            var Q130;
            Q130=sQuery(id+"F2.wireOp",EDGE,"E116");
            var Q131;
            Q131=sQuery(id+"F2.wireOp",EDGE,"E153");
            var Q132;
            Q132=sQuery(id+"F2.wireOp",EDGE,"E179");
            var Q133;
            Q133=sQuery(id+"F2.wireOp",EDGE,"E67");
            var Q134;
            Q134=sQuery(id+"F2.wireOp",EDGE,"E35");
            var Q135;
            Q135=sQuery(id+"F2.wireOp",EDGE,"E60");
            var Q136;
            Q136=sQuery(id+"F2.wireOp",EDGE,"E201");
            var Q137;
            Q137=sQuery(id+"F2.wireOp",EDGE,"E108");
            var Q138;
            Q138=sQuery(id+"F2.wireOp",EDGE,"E120");
            var Q139;
            Q139=sQuery(id+"F2.wireOp",EDGE,"E126");
            var Q140;
            Q140=sQuery(id+"F2.wireOp",EDGE,"E188");
            var Q141;
            Q141=sQuery(id+"F2.wireOp",EDGE,"E92");
            var Q142;
            Q142=sQuery(id+"F2.wireOp",EDGE,"E85");
            var Q143;
            Q143=sQuery(id+"F2.wireOp",EDGE,"E117");
            var Q144;
            Q144=sQuery(id+"F2.wireOp",EDGE,"E24");
            var Q145;
            Q145=sQuery(id+"F2.wireOp",EDGE,"E32");
            var Q146;
            Q146=sQuery(id+"F2.wireOp",EDGE,"E70");
            var Q147;
            Q147=sQuery(id+"F2.wireOp",EDGE,"E61");
            var Q148;
            Q148=sQuery(id+"F2.wireOp",EDGE,"E125");
            var Q149;
            Q149=sQuery(id+"F2.wireOp",EDGE,"E118");
            var Q150;
            Q150=sQuery(id+"F2.wireOp",EDGE,"E102");
            var Q151;
            Q151=sQuery(id+"F2.wireOp",EDGE,"E109");
            var Q152;
            Q152=sQuery(id+"F2.wireOp",EDGE,"E93");
            var Q153;
            Q153=sQuery(id+"F2.wireOp",EDGE,"E198");
            var Q154;
            Q154=sQuery(id+"F2.wireOp",EDGE,"E166");
            var Q155;
            Q155=sQuery(id+"F2.wireOp",EDGE,"E12");
            var Q156;
            Q156=sQuery(id+"F2.wireOp",EDGE,"E13");
            var Q157;
            Q157=sQuery(id+"F2.wireOp",EDGE,"E25");
            var Q158;
            Q158=sQuery(id+"F2.wireOp",EDGE,"E121");
            var Q159;
            Q159=sQuery(id+"F2.wireOp",EDGE,"E105");
            var Q160;
            Q160=sQuery(id+"F2.wireOp",EDGE,"E20");
            var Q161;
            Q161=sQuery(id+"F2.wireOp",EDGE,"E33");
            var Q162;
            Q162=sQuery(id+"F2.wireOp",EDGE,"E113");
            var Q163;
            Q163=sQuery(id+"F2.wireOp",EDGE,"E129");
            var Q164;
            Q164=sQuery(id+"F2.wireOp",EDGE,"E138");
            var Q165;
            Q165=sQuery(id+"F2.wireOp",EDGE,"E122");
            var Q166;
            Q166=sQuery(id+"F2.wireOp",EDGE,"E202");
            var Q167;
            Q167=sQuery(id+"F2.wireOp",EDGE,"E186");
            var Q168;
            Q168=sQuery(id+"F2.wireOp",EDGE,"E154");
            var Q169;
            Q169=sQuery(id+"F2.wireOp",EDGE,"E34");
            var Q170;
            Q170=sQuery(id+"F2.wireOp",EDGE,"E66");
            var Q171;
            Q171=sQuery(id+"F2.wireOp",EDGE,"E162");
            var Q172;
            Q172=sQuery(id+"F2.wireOp",EDGE,"E194");
            var Q173;
            Q173=sQuery(id+"F2.wireOp",EDGE,"E30");
            var Q174;
            Q174=sQuery(id+"F2.wireOp",EDGE,"E71");
            var Q175;
            Q175=sQuery(id+"F2.wireOp",EDGE,"E119");
            var Q176;
            Q176=sQuery(id+"F2.wireOp",EDGE,"E199");
            var Q177;
            Q177=sQuery(id+"F2.wireOp",EDGE,"E79");
            var Q178;
            Q178=sQuery(id+"F2.wireOp",EDGE,"E133");
            var Q179;
            Q179=sQuery(id+"F2.wireOp",EDGE,"E131");
            var Q180;
            Q180=sQuery(id+"F2.wireOp",EDGE,"E172");
            var Q181;
            Q181=sQuery(id+"F2.wireOp",EDGE,"E53");
            var Q182;
            Q182=sQuery(id+"F2.wireOp",EDGE,"E127");
            var Q183;
            Q183=sQuery(id+"F2.wireOp",EDGE,"E168");
            var Q184;
            Q184=sQuery(id+"F2.wireOp",EDGE,"E174");
            var Q185;
            Q185=sQuery(id+"F2.wireOp",EDGE,"E115");
            var Q186;
            Q186=sQuery(id+"F2.wireOp",EDGE,"E76");
            var Q187;
            Q187=sQuery(id+"F2.wireOp",EDGE,"E159");
            var Q188;
            Q188=sQuery(id+"F2.wireOp",EDGE,"E132");
            var Q189;
            Q189=sQuery(id+"F2.wireOp",EDGE,"E80");
            var Q190;
            Q190=sQuery(id+"F2.wireOp",EDGE,"E64");
            var Q191;
            Q191=sQuery(id+"F2.wireOp",EDGE,"E160");
            var Q192;
            Q192=sQuery(id+"F2.wireOp",EDGE,"E144");
            var Q193;
            Q193=sQuery(id+"F2.wireOp",EDGE,"E128");
            var Q194;
            Q194=sQuery(id+"F2.wireOp",EDGE,"E9");
            var Q195;
            Q195=sQuery(id+"F2.wireOp",EDGE,"E54");
            var Q196;
            Q196=sQuery(id+"F2.wireOp",EDGE,"E45");
            var Q197;
            Q197=sQuery(id+"F2.wireOp",EDGE,"E10");
            var Q198;
            Q198=sQuery(id+"F2.wireOp",EDGE,"E173");
            var Q199;
            Q199=sQuery(id+"F2.wireOp",EDGE,"E106");
            var Q200;
            Q200=sQuery(id+"F2.wireOp",EDGE,"E114");
            var Q201;
            Q201=sQuery(id+"F2.wireOp",EDGE,"E107");
            var Q202;
            Q202=sQuery(id+"F2.wireOp",EDGE,"E91");
            var Q203;
            Q203=sQuery(id+"F2.wireOp",EDGE,"E63");
            var Q204;
            Q204=sQuery(id+"F2.wireOp",EDGE,"E185");
            var Q205;
            Q205=sQuery(id+"F2.wireOp",EDGE,"E184");
            var Q206;
            Q206=sQuery(id+"F2.wireOp",EDGE,"E192");
            var Q207;
            Q207=sQuery(id+"F2.wireOp",EDGE,"E56");
            var Q208;
            Q208=sQuery(id+"F2.wireOp",EDGE,"E143");
            var Q209;
            Q209=sQuery(id+"F2.wireOp",EDGE,"E141");
            var Q210;
            Q210=sQuery(id+"F2.wireOp",EDGE,"E57");
            var Q211;
            Q211=sQuery(id+"F2.wireOp",EDGE,"E14");
            var Q212;
            Q212=sQuery(id+"F2.wireOp",EDGE,"E15");
            var Q213;
            Q213=sQuery(id+"F2.wireOp",EDGE,"E16");
            var Q214;
            Q214=sQuery(id+"F2.wireOp",EDGE,"E26");
            var Q215;
            Q215=sQuery(id+"F2.wireOp",EDGE,"E142");
            extrude(context, id + "F3", {"entities" : qUnion([Q0, Q1, Q2, Q3, Q4, Q5, Q6, Q7, Q8, Q9, Q10, Q11, Q12, Q13, Q14, Q15, Q16, Q17, Q18]), "surfaceEntities" : qUnion([Q19, Q20, Q21, Q22, Q23, Q24, Q25, Q26, Q27, Q28, Q29, Q30, Q31, Q32, Q33, Q34, Q35, Q36, Q37, Q38, Q39, Q40, Q41, Q42, Q43, Q44, Q45, Q46, Q47, Q48, Q49, Q50, Q51, Q52, Q53, Q54, Q55, Q56, Q57, Q58, Q59, Q60, Q61, Q62, Q63, Q64, Q65, Q66, Q67, Q68, Q69, Q70, Q71, Q72, Q73, Q74, Q75, Q76, Q77, Q78, Q79, Q80, Q81, Q82, Q83, Q84, Q85, Q86, Q87, Q88, Q89, Q90, Q91, Q92, Q93, Q94, Q95, Q96, Q97, Q98, Q99, Q100, Q101, Q102, Q103, Q104, Q105, Q106, Q107, Q108, Q109, Q110, Q111, Q112, Q113, Q114, Q115, Q116, Q117, Q118, Q119, Q120, Q121, Q122, Q123, Q124, Q125, Q126, Q127, Q128, Q129, Q130, Q131, Q132, Q133, Q134, Q135, Q136, Q137, Q138, Q139, Q140, Q141, Q142, Q143, Q144, Q145, Q146, Q147, Q148, Q149, Q150, Q151, Q152, Q153, Q154, Q155, Q156, Q157, Q158, Q159, Q160, Q161, Q162, Q163, Q164, Q165, Q166, Q167, Q168, Q169, Q170, Q171, Q172, Q173, Q174, Q175, Q176, Q177, Q178, Q179, Q180, Q181, Q182, Q183, Q184, Q185, Q186, Q187, Q188, Q189, Q190, Q191, Q192, Q193, Q194, Q195, Q196, Q197, Q198, Q199, Q200, Q201, Q202, Q203, Q204, Q205, Q206, Q207, Q208, Q209, Q210, Q211, Q212, Q213, Q214, Q215]), "depth" : 25 * mm, "offsetDistance" : 25 * mm, "hasSecondDirection" : true, "secondDirectionOppositeDirection" : true, "secondDirectionDepth" : 25 * mm});
        }
        {
            var Q0;
            Q0=makeQuery(id+"F3.opExtrude","SWEPT_BODY",BODY,{"disambiguationData":[OSD([sQuery(id+"F2.wireOp",EDGE,"E101"),sQuery(id+"F2.wireOp",EDGE,"E102"),sQuery(id+"F2.wireOp",EDGE,"E103"),sQuery(id+"F2.wireOp",EDGE,"E104"),sQuery(id+"F2.wireOp",EDGE,"E105"),sQuery(id+"F2.wireOp",EDGE,"E106"),sQuery(id+"F2.wireOp",EDGE,"E107"),sQuery(id+"F2.wireOp",EDGE,"E108"),sQuery(id+"F2.wireOp",EDGE,"E109"),sQuery(id+"F2.wireOp",EDGE,"E110"),sQuery(id+"F2.wireOp",EDGE,"E111"),sQuery(id+"F2.wireOp",EDGE,"E112"),sQuery(id+"F2.wireOp",EDGE,"E113"),sQuery(id+"F2.wireOp",EDGE,"E114"),sQuery(id+"F2.wireOp",EDGE,"E115"),sQuery(id+"F2.wireOp",EDGE,"E116"),sQuery(id+"F2.wireOp",EDGE,"E117"),sQuery(id+"F2.wireOp",EDGE,"E118"),sQuery(id+"F2.wireOp",EDGE,"E119"),sQuery(id+"F2.wireOp",EDGE,"E120"),sQuery(id+"F2.wireOp",EDGE,"E121"),sQuery(id+"F2.wireOp",EDGE,"E122"),sQuery(id+"F2.wireOp",EDGE,"E123"),sQuery(id+"F2.wireOp",EDGE,"E124"),sQuery(id+"F2.wireOp",EDGE,"E125"),sQuery(id+"F2.wireOp",EDGE,"E126")])]});
            var Q1;
            Q1=makeQuery(id+"F3.opExtrude","SWEPT_BODY",BODY,{"disambiguationData":[OSD([sQuery(id+"F2.wireOp",EDGE,"E127"),sQuery(id+"F2.wireOp",EDGE,"E128"),sQuery(id+"F2.wireOp",EDGE,"E129"),sQuery(id+"F2.wireOp",EDGE,"E130"),sQuery(id+"F2.wireOp",EDGE,"E131"),sQuery(id+"F2.wireOp",EDGE,"E132"),sQuery(id+"F2.wireOp",EDGE,"E133"),sQuery(id+"F2.wireOp",EDGE,"E134"),sQuery(id+"F2.wireOp",EDGE,"E135"),sQuery(id+"F2.wireOp",EDGE,"E136"),sQuery(id+"F2.wireOp",EDGE,"E137"),sQuery(id+"F2.wireOp",EDGE,"E138"),sQuery(id+"F2.wireOp",EDGE,"E139"),sQuery(id+"F2.wireOp",EDGE,"E140"),sQuery(id+"F2.wireOp",EDGE,"E141"),sQuery(id+"F2.wireOp",EDGE,"E142"),sQuery(id+"F2.wireOp",EDGE,"E143"),sQuery(id+"F2.wireOp",EDGE,"E144")])]});
            var Q2;
            Q2=makeQuery(id+"F3.opExtrude","SWEPT_BODY",BODY,{"disambiguationData":[OSD([sQuery(id+"F2.wireOp",EDGE,"E157"),sQuery(id+"F2.wireOp",EDGE,"E158"),sQuery(id+"F2.wireOp",EDGE,"E159"),sQuery(id+"F2.wireOp",EDGE,"E160"),sQuery(id+"F2.wireOp",EDGE,"E161"),sQuery(id+"F2.wireOp",EDGE,"E162"),sQuery(id+"F2.wireOp",EDGE,"E163"),sQuery(id+"F2.wireOp",EDGE,"E164"),sQuery(id+"F2.wireOp",EDGE,"E165"),sQuery(id+"F2.wireOp",EDGE,"E166"),sQuery(id+"F2.wireOp",EDGE,"E167"),sQuery(id+"F2.wireOp",EDGE,"E168"),sQuery(id+"F2.wireOp",EDGE,"E169"),sQuery(id+"F2.wireOp",EDGE,"E170"),sQuery(id+"F2.wireOp",EDGE,"E171")])]});
            var Q3;
            Q3=makeQuery(id+"F3.opExtrude","SWEPT_BODY",BODY,{"disambiguationData":[OSD([sQuery(id+"F2.wireOp",EDGE,"E145"),sQuery(id+"F2.wireOp",EDGE,"E146"),sQuery(id+"F2.wireOp",EDGE,"E147"),sQuery(id+"F2.wireOp",EDGE,"E148"),sQuery(id+"F2.wireOp",EDGE,"E149"),sQuery(id+"F2.wireOp",EDGE,"E150"),sQuery(id+"F2.wireOp",EDGE,"E151"),sQuery(id+"F2.wireOp",EDGE,"E152"),sQuery(id+"F2.wireOp",EDGE,"E153"),sQuery(id+"F2.wireOp",EDGE,"E154"),sQuery(id+"F2.wireOp",EDGE,"E155"),sQuery(id+"F2.wireOp",EDGE,"E156")])]});
            var Q4;
            Q4=makeQuery(id+"F3.opExtrude","SWEPT_BODY",BODY,{"disambiguationData":[OSD([sQuery(id+"F2.wireOp",EDGE,"E80"),sQuery(id+"F2.wireOp",EDGE,"E81"),sQuery(id+"F2.wireOp",EDGE,"E82"),sQuery(id+"F2.wireOp",EDGE,"E83"),sQuery(id+"F2.wireOp",EDGE,"E84"),sQuery(id+"F2.wireOp",EDGE,"E85"),sQuery(id+"F2.wireOp",EDGE,"E86"),sQuery(id+"F2.wireOp",EDGE,"E87"),sQuery(id+"F2.wireOp",EDGE,"E88"),sQuery(id+"F2.wireOp",EDGE,"E89"),sQuery(id+"F2.wireOp",EDGE,"E90"),sQuery(id+"F2.wireOp",EDGE,"E91"),sQuery(id+"F2.wireOp",EDGE,"E92"),sQuery(id+"F2.wireOp",EDGE,"E93"),sQuery(id+"F2.wireOp",EDGE,"E94"),sQuery(id+"F2.wireOp",EDGE,"E95"),sQuery(id+"F2.wireOp",EDGE,"E96"),sQuery(id+"F2.wireOp",EDGE,"E97"),sQuery(id+"F2.wireOp",EDGE,"E98"),sQuery(id+"F2.wireOp",EDGE,"E99"),sQuery(id+"F2.wireOp",EDGE,"E100")])]});
            var Q5;
            Q5=makeQuery(id+"F3.opExtrude","SWEPT_BODY",BODY,{"disambiguationData":[OSD([sQuery(id+"F2.wireOp",EDGE,"E36"),sQuery(id+"F2.wireOp",EDGE,"E37"),sQuery(id+"F2.wireOp",EDGE,"E38"),sQuery(id+"F2.wireOp",EDGE,"E39"),sQuery(id+"F2.wireOp",EDGE,"E40"),sQuery(id+"F2.wireOp",EDGE,"E41"),sQuery(id+"F2.wireOp",EDGE,"E42"),sQuery(id+"F2.wireOp",EDGE,"E43"),sQuery(id+"F2.wireOp",EDGE,"E44"),sQuery(id+"F2.wireOp",EDGE,"E45"),sQuery(id+"F2.wireOp",EDGE,"E46"),sQuery(id+"F2.wireOp",EDGE,"E47"),sQuery(id+"F2.wireOp",EDGE,"E48"),sQuery(id+"F2.wireOp",EDGE,"E49"),sQuery(id+"F2.wireOp",EDGE,"E50"),sQuery(id+"F2.wireOp",EDGE,"E51"),sQuery(id+"F2.wireOp",EDGE,"E52")])]});
            var Q6;
            Q6=makeQuery(id+"F3.opExtrude","SWEPT_BODY",BODY,{"disambiguationData":[OSD([sQuery(id+"F2.wireOp",EDGE,"E53"),sQuery(id+"F2.wireOp",EDGE,"E54"),sQuery(id+"F2.wireOp",EDGE,"E55"),sQuery(id+"F2.wireOp",EDGE,"E56"),sQuery(id+"F2.wireOp",EDGE,"E57"),sQuery(id+"F2.wireOp",EDGE,"E58"),sQuery(id+"F2.wireOp",EDGE,"E59"),sQuery(id+"F2.wireOp",EDGE,"E60"),sQuery(id+"F2.wireOp",EDGE,"E61"),sQuery(id+"F2.wireOp",EDGE,"E62"),sQuery(id+"F2.wireOp",EDGE,"E63"),sQuery(id+"F2.wireOp",EDGE,"E64"),sQuery(id+"F2.wireOp",EDGE,"E65"),sQuery(id+"F2.wireOp",EDGE,"E66"),sQuery(id+"F2.wireOp",EDGE,"E67"),sQuery(id+"F2.wireOp",EDGE,"E68"),sQuery(id+"F2.wireOp",EDGE,"E69"),sQuery(id+"F2.wireOp",EDGE,"E70"),sQuery(id+"F2.wireOp",EDGE,"E71"),sQuery(id+"F2.wireOp",EDGE,"E72"),sQuery(id+"F2.wireOp",EDGE,"E73"),sQuery(id+"F2.wireOp",EDGE,"E74"),sQuery(id+"F2.wireOp",EDGE,"E75"),sQuery(id+"F2.wireOp",EDGE,"E76"),sQuery(id+"F2.wireOp",EDGE,"E77"),sQuery(id+"F2.wireOp",EDGE,"E78"),sQuery(id+"F2.wireOp",EDGE,"E79")])]});
            var Q7;
            Q7=makeQuery(id+"F3.opExtrude","SWEPT_BODY",BODY,{"disambiguationData":[OSD([sQuery(id+"F2.wireOp",EDGE,"E8"),sQuery(id+"F2.wireOp",EDGE,"E9"),sQuery(id+"F2.wireOp",EDGE,"E10"),sQuery(id+"F2.wireOp",EDGE,"E11"),sQuery(id+"F2.wireOp",EDGE,"E12"),sQuery(id+"F2.wireOp",EDGE,"E13"),sQuery(id+"F2.wireOp",EDGE,"E14"),sQuery(id+"F2.wireOp",EDGE,"E15"),sQuery(id+"F2.wireOp",EDGE,"E16"),sQuery(id+"F2.wireOp",EDGE,"E17"),sQuery(id+"F2.wireOp",EDGE,"E18"),sQuery(id+"F2.wireOp",EDGE,"E19"),sQuery(id+"F2.wireOp",EDGE,"E20"),sQuery(id+"F2.wireOp",EDGE,"E21"),sQuery(id+"F2.wireOp",EDGE,"E22"),sQuery(id+"F2.wireOp",EDGE,"E23"),sQuery(id+"F2.wireOp",EDGE,"E24"),sQuery(id+"F2.wireOp",EDGE,"E25"),sQuery(id+"F2.wireOp",EDGE,"E26"),sQuery(id+"F2.wireOp",EDGE,"E27"),sQuery(id+"F2.wireOp",EDGE,"E28"),sQuery(id+"F2.wireOp",EDGE,"E29"),sQuery(id+"F2.wireOp",EDGE,"E30"),sQuery(id+"F2.wireOp",EDGE,"E31"),sQuery(id+"F2.wireOp",EDGE,"E32"),sQuery(id+"F2.wireOp",EDGE,"E33"),sQuery(id+"F2.wireOp",EDGE,"E34"),sQuery(id+"F2.wireOp",EDGE,"E35")])]});
            var Q8;
            Q8=makeQuery(id+"F3.opExtrude","SWEPT_BODY",BODY,{"disambiguationData":[OSD([sQuery(id+"F2.wireOp",EDGE,"E193"),sQuery(id+"F2.wireOp",EDGE,"E194"),sQuery(id+"F2.wireOp",EDGE,"E195"),sQuery(id+"F2.wireOp",EDGE,"E196"),sQuery(id+"F2.wireOp",EDGE,"E197"),sQuery(id+"F2.wireOp",EDGE,"E198"),sQuery(id+"F2.wireOp",EDGE,"E199"),sQuery(id+"F2.wireOp",EDGE,"E200")])]});
            var Q9;
            Q9=makeQuery(id+"F3.opExtrude","SWEPT_BODY",BODY,{"disambiguationData":[OSD([sQuery(id+"F2.wireOp",EDGE,"E184"),sQuery(id+"F2.wireOp",EDGE,"E185"),sQuery(id+"F2.wireOp",EDGE,"E186"),sQuery(id+"F2.wireOp",EDGE,"E187"),sQuery(id+"F2.wireOp",EDGE,"E188"),sQuery(id+"F2.wireOp",EDGE,"E189"),sQuery(id+"F2.wireOp",EDGE,"E190"),sQuery(id+"F2.wireOp",EDGE,"E191"),sQuery(id+"F2.wireOp",EDGE,"E192")])]});
            var Q10;
            Q10=makeQuery(id+"F3.opExtrude","SWEPT_BODY",BODY,{"disambiguationData":[OSD([sQuery(id+"F2.wireOp",EDGE,"E201"),sQuery(id+"F2.wireOp",EDGE,"E202"),sQuery(id+"F2.wireOp",EDGE,"E203"),sQuery(id+"F2.wireOp",EDGE,"E204")])]});
            var Q11;
            Q11=makeQuery(id+"F3.opExtrude","SWEPT_BODY",BODY,{"disambiguationData":[OSD([sQuery(id+"F2.wireOp",EDGE,"E172"),sQuery(id+"F2.wireOp",EDGE,"E173"),sQuery(id+"F2.wireOp",EDGE,"E174"),sQuery(id+"F2.wireOp",EDGE,"E175"),sQuery(id+"F2.wireOp",EDGE,"E176"),sQuery(id+"F2.wireOp",EDGE,"E177"),sQuery(id+"F2.wireOp",EDGE,"E178"),sQuery(id+"F2.wireOp",EDGE,"E179"),sQuery(id+"F2.wireOp",EDGE,"E180"),sQuery(id+"F2.wireOp",EDGE,"E181"),sQuery(id+"F2.wireOp",EDGE,"E182"),sQuery(id+"F2.wireOp",EDGE,"E183")])]});
            var Q12;
            Q12=qCreatedBy(makeId("Origin.pointOp"),VERTEX);
            transform(context, id + "F4", {"entities" : qUnion([Q0, Q1, Q2, Q3, Q4, Q5, Q6, Q7, Q8, Q9, Q10, Q11]), "transformType" : TransformType.SCALE_UNIFORMLY, "scale" : .15, "scalePoint" : qUnion([Q12]), "makeCopy" : false});
        }
        {
            var Q0;
            Q0=makeQuery(id+"F3.opExtrude","SWEPT_BODY",BODY,{"disambiguationData":[OSD([sQuery(id+"F2.wireOp",EDGE,"E8"),sQuery(id+"F2.wireOp",EDGE,"E9"),sQuery(id+"F2.wireOp",EDGE,"E10"),sQuery(id+"F2.wireOp",EDGE,"E11"),sQuery(id+"F2.wireOp",EDGE,"E12"),sQuery(id+"F2.wireOp",EDGE,"E13"),sQuery(id+"F2.wireOp",EDGE,"E14"),sQuery(id+"F2.wireOp",EDGE,"E15"),sQuery(id+"F2.wireOp",EDGE,"E16"),sQuery(id+"F2.wireOp",EDGE,"E17"),sQuery(id+"F2.wireOp",EDGE,"E18"),sQuery(id+"F2.wireOp",EDGE,"E19"),sQuery(id+"F2.wireOp",EDGE,"E20"),sQuery(id+"F2.wireOp",EDGE,"E21"),sQuery(id+"F2.wireOp",EDGE,"E22"),sQuery(id+"F2.wireOp",EDGE,"E23"),sQuery(id+"F2.wireOp",EDGE,"E24"),sQuery(id+"F2.wireOp",EDGE,"E25"),sQuery(id+"F2.wireOp",EDGE,"E26"),sQuery(id+"F2.wireOp",EDGE,"E27"),sQuery(id+"F2.wireOp",EDGE,"E28"),sQuery(id+"F2.wireOp",EDGE,"E29"),sQuery(id+"F2.wireOp",EDGE,"E30"),sQuery(id+"F2.wireOp",EDGE,"E31"),sQuery(id+"F2.wireOp",EDGE,"E32"),sQuery(id+"F2.wireOp",EDGE,"E33"),sQuery(id+"F2.wireOp",EDGE,"E34"),sQuery(id+"F2.wireOp",EDGE,"E35")])]});
            var Q1;
            Q1=makeQuery(id+"F3.opExtrude","SWEPT_BODY",BODY,{"disambiguationData":[OSD([sQuery(id+"F2.wireOp",EDGE,"E36"),sQuery(id+"F2.wireOp",EDGE,"E37"),sQuery(id+"F2.wireOp",EDGE,"E38"),sQuery(id+"F2.wireOp",EDGE,"E39"),sQuery(id+"F2.wireOp",EDGE,"E40"),sQuery(id+"F2.wireOp",EDGE,"E41"),sQuery(id+"F2.wireOp",EDGE,"E42"),sQuery(id+"F2.wireOp",EDGE,"E43"),sQuery(id+"F2.wireOp",EDGE,"E44"),sQuery(id+"F2.wireOp",EDGE,"E45"),sQuery(id+"F2.wireOp",EDGE,"E46"),sQuery(id+"F2.wireOp",EDGE,"E47"),sQuery(id+"F2.wireOp",EDGE,"E48"),sQuery(id+"F2.wireOp",EDGE,"E49"),sQuery(id+"F2.wireOp",EDGE,"E50"),sQuery(id+"F2.wireOp",EDGE,"E51"),sQuery(id+"F2.wireOp",EDGE,"E52")])]});
            var Q2;
            Q2=makeQuery(id+"F3.opExtrude","SWEPT_BODY",BODY,{"disambiguationData":[OSD([sQuery(id+"F2.wireOp",EDGE,"E53"),sQuery(id+"F2.wireOp",EDGE,"E54"),sQuery(id+"F2.wireOp",EDGE,"E55"),sQuery(id+"F2.wireOp",EDGE,"E56"),sQuery(id+"F2.wireOp",EDGE,"E57"),sQuery(id+"F2.wireOp",EDGE,"E58"),sQuery(id+"F2.wireOp",EDGE,"E59"),sQuery(id+"F2.wireOp",EDGE,"E60"),sQuery(id+"F2.wireOp",EDGE,"E61"),sQuery(id+"F2.wireOp",EDGE,"E62"),sQuery(id+"F2.wireOp",EDGE,"E63"),sQuery(id+"F2.wireOp",EDGE,"E64"),sQuery(id+"F2.wireOp",EDGE,"E65"),sQuery(id+"F2.wireOp",EDGE,"E66"),sQuery(id+"F2.wireOp",EDGE,"E67"),sQuery(id+"F2.wireOp",EDGE,"E68"),sQuery(id+"F2.wireOp",EDGE,"E69"),sQuery(id+"F2.wireOp",EDGE,"E70"),sQuery(id+"F2.wireOp",EDGE,"E71"),sQuery(id+"F2.wireOp",EDGE,"E72"),sQuery(id+"F2.wireOp",EDGE,"E73"),sQuery(id+"F2.wireOp",EDGE,"E74"),sQuery(id+"F2.wireOp",EDGE,"E75"),sQuery(id+"F2.wireOp",EDGE,"E76"),sQuery(id+"F2.wireOp",EDGE,"E77"),sQuery(id+"F2.wireOp",EDGE,"E78"),sQuery(id+"F2.wireOp",EDGE,"E79")])]});
            var Q3;
            Q3=makeQuery(id+"F3.opExtrude","SWEPT_BODY",BODY,{"disambiguationData":[OSD([sQuery(id+"F2.wireOp",EDGE,"E80"),sQuery(id+"F2.wireOp",EDGE,"E81"),sQuery(id+"F2.wireOp",EDGE,"E82"),sQuery(id+"F2.wireOp",EDGE,"E83"),sQuery(id+"F2.wireOp",EDGE,"E84"),sQuery(id+"F2.wireOp",EDGE,"E85"),sQuery(id+"F2.wireOp",EDGE,"E86"),sQuery(id+"F2.wireOp",EDGE,"E87"),sQuery(id+"F2.wireOp",EDGE,"E88"),sQuery(id+"F2.wireOp",EDGE,"E89"),sQuery(id+"F2.wireOp",EDGE,"E90"),sQuery(id+"F2.wireOp",EDGE,"E91"),sQuery(id+"F2.wireOp",EDGE,"E92"),sQuery(id+"F2.wireOp",EDGE,"E93"),sQuery(id+"F2.wireOp",EDGE,"E94"),sQuery(id+"F2.wireOp",EDGE,"E95"),sQuery(id+"F2.wireOp",EDGE,"E96"),sQuery(id+"F2.wireOp",EDGE,"E97"),sQuery(id+"F2.wireOp",EDGE,"E98"),sQuery(id+"F2.wireOp",EDGE,"E99"),sQuery(id+"F2.wireOp",EDGE,"E100")])]});
            var Q4;
            Q4=makeQuery(id+"F3.opExtrude","SWEPT_BODY",BODY,{"disambiguationData":[OSD([sQuery(id+"F2.wireOp",EDGE,"E101"),sQuery(id+"F2.wireOp",EDGE,"E102"),sQuery(id+"F2.wireOp",EDGE,"E103"),sQuery(id+"F2.wireOp",EDGE,"E104"),sQuery(id+"F2.wireOp",EDGE,"E105"),sQuery(id+"F2.wireOp",EDGE,"E106"),sQuery(id+"F2.wireOp",EDGE,"E107"),sQuery(id+"F2.wireOp",EDGE,"E108"),sQuery(id+"F2.wireOp",EDGE,"E109"),sQuery(id+"F2.wireOp",EDGE,"E110"),sQuery(id+"F2.wireOp",EDGE,"E111"),sQuery(id+"F2.wireOp",EDGE,"E112"),sQuery(id+"F2.wireOp",EDGE,"E113"),sQuery(id+"F2.wireOp",EDGE,"E114"),sQuery(id+"F2.wireOp",EDGE,"E115"),sQuery(id+"F2.wireOp",EDGE,"E116"),sQuery(id+"F2.wireOp",EDGE,"E117"),sQuery(id+"F2.wireOp",EDGE,"E118"),sQuery(id+"F2.wireOp",EDGE,"E119"),sQuery(id+"F2.wireOp",EDGE,"E120"),sQuery(id+"F2.wireOp",EDGE,"E121"),sQuery(id+"F2.wireOp",EDGE,"E122"),sQuery(id+"F2.wireOp",EDGE,"E123"),sQuery(id+"F2.wireOp",EDGE,"E124"),sQuery(id+"F2.wireOp",EDGE,"E125"),sQuery(id+"F2.wireOp",EDGE,"E126")])]});
            var Q5;
            Q5=makeQuery(id+"F3.opExtrude","SWEPT_BODY",BODY,{"disambiguationData":[OSD([sQuery(id+"F2.wireOp",EDGE,"E127"),sQuery(id+"F2.wireOp",EDGE,"E128"),sQuery(id+"F2.wireOp",EDGE,"E129"),sQuery(id+"F2.wireOp",EDGE,"E130"),sQuery(id+"F2.wireOp",EDGE,"E131"),sQuery(id+"F2.wireOp",EDGE,"E132"),sQuery(id+"F2.wireOp",EDGE,"E133"),sQuery(id+"F2.wireOp",EDGE,"E134"),sQuery(id+"F2.wireOp",EDGE,"E135"),sQuery(id+"F2.wireOp",EDGE,"E136"),sQuery(id+"F2.wireOp",EDGE,"E137"),sQuery(id+"F2.wireOp",EDGE,"E138"),sQuery(id+"F2.wireOp",EDGE,"E139"),sQuery(id+"F2.wireOp",EDGE,"E140"),sQuery(id+"F2.wireOp",EDGE,"E141"),sQuery(id+"F2.wireOp",EDGE,"E142"),sQuery(id+"F2.wireOp",EDGE,"E143"),sQuery(id+"F2.wireOp",EDGE,"E144")])]});
            var Q6;
            Q6=makeQuery(id+"F3.opExtrude","SWEPT_BODY",BODY,{"disambiguationData":[OSD([sQuery(id+"F2.wireOp",EDGE,"E145"),sQuery(id+"F2.wireOp",EDGE,"E146"),sQuery(id+"F2.wireOp",EDGE,"E147"),sQuery(id+"F2.wireOp",EDGE,"E148"),sQuery(id+"F2.wireOp",EDGE,"E149"),sQuery(id+"F2.wireOp",EDGE,"E150"),sQuery(id+"F2.wireOp",EDGE,"E151"),sQuery(id+"F2.wireOp",EDGE,"E152"),sQuery(id+"F2.wireOp",EDGE,"E153"),sQuery(id+"F2.wireOp",EDGE,"E154"),sQuery(id+"F2.wireOp",EDGE,"E155"),sQuery(id+"F2.wireOp",EDGE,"E156")])]});
            var Q7;
            Q7=makeQuery(id+"F3.opExtrude","SWEPT_BODY",BODY,{"disambiguationData":[OSD([sQuery(id+"F2.wireOp",EDGE,"E157"),sQuery(id+"F2.wireOp",EDGE,"E158"),sQuery(id+"F2.wireOp",EDGE,"E159"),sQuery(id+"F2.wireOp",EDGE,"E160"),sQuery(id+"F2.wireOp",EDGE,"E161"),sQuery(id+"F2.wireOp",EDGE,"E162"),sQuery(id+"F2.wireOp",EDGE,"E163"),sQuery(id+"F2.wireOp",EDGE,"E164"),sQuery(id+"F2.wireOp",EDGE,"E165"),sQuery(id+"F2.wireOp",EDGE,"E166"),sQuery(id+"F2.wireOp",EDGE,"E167"),sQuery(id+"F2.wireOp",EDGE,"E168"),sQuery(id+"F2.wireOp",EDGE,"E169"),sQuery(id+"F2.wireOp",EDGE,"E170"),sQuery(id+"F2.wireOp",EDGE,"E171")])]});
            var Q8;
            Q8=makeQuery(id+"F3.opExtrude","SWEPT_BODY",BODY,{"disambiguationData":[OSD([sQuery(id+"F2.wireOp",EDGE,"E172"),sQuery(id+"F2.wireOp",EDGE,"E173"),sQuery(id+"F2.wireOp",EDGE,"E174"),sQuery(id+"F2.wireOp",EDGE,"E175"),sQuery(id+"F2.wireOp",EDGE,"E176"),sQuery(id+"F2.wireOp",EDGE,"E177"),sQuery(id+"F2.wireOp",EDGE,"E178"),sQuery(id+"F2.wireOp",EDGE,"E179"),sQuery(id+"F2.wireOp",EDGE,"E180"),sQuery(id+"F2.wireOp",EDGE,"E181"),sQuery(id+"F2.wireOp",EDGE,"E182"),sQuery(id+"F2.wireOp",EDGE,"E183")])]});
            var Q9;
            Q9=makeQuery(id+"F3.opExtrude","SWEPT_BODY",BODY,{"disambiguationData":[OSD([sQuery(id+"F2.wireOp",EDGE,"E184"),sQuery(id+"F2.wireOp",EDGE,"E185"),sQuery(id+"F2.wireOp",EDGE,"E186"),sQuery(id+"F2.wireOp",EDGE,"E187"),sQuery(id+"F2.wireOp",EDGE,"E188"),sQuery(id+"F2.wireOp",EDGE,"E189"),sQuery(id+"F2.wireOp",EDGE,"E190"),sQuery(id+"F2.wireOp",EDGE,"E191"),sQuery(id+"F2.wireOp",EDGE,"E192")])]});
            var Q10;
            Q10=makeQuery(id+"F3.opExtrude","SWEPT_BODY",BODY,{"disambiguationData":[OSD([sQuery(id+"F2.wireOp",EDGE,"E193"),sQuery(id+"F2.wireOp",EDGE,"E194"),sQuery(id+"F2.wireOp",EDGE,"E195"),sQuery(id+"F2.wireOp",EDGE,"E196"),sQuery(id+"F2.wireOp",EDGE,"E197"),sQuery(id+"F2.wireOp",EDGE,"E198"),sQuery(id+"F2.wireOp",EDGE,"E199"),sQuery(id+"F2.wireOp",EDGE,"E200")])]});
            var Q11;
            Q11=makeQuery(id+"F3.opExtrude","SWEPT_BODY",BODY,{"disambiguationData":[OSD([sQuery(id+"F2.wireOp",EDGE,"E201"),sQuery(id+"F2.wireOp",EDGE,"E202"),sQuery(id+"F2.wireOp",EDGE,"E203"),sQuery(id+"F2.wireOp",EDGE,"E204")])]});
            var Q12;
            Q12=makeQuery(id+"F1.opExtrude","SWEPT_BODY",BODY,{"disambiguationData":[OSD([sQuery(id+"F0.wireOp",EDGE,"E0"),sQuery(id+"F0.wireOp",EDGE,"E1"),sQuery(id+"F0.wireOp",EDGE,"E2"),sQuery(id+"F0.wireOp",EDGE,"E3"),sQuery(id+"F0.wireOp",EDGE,"E4"),sQuery(id+"F0.wireOp",EDGE,"E5.filletArc"),sQuery(id+"F0.wireOp",EDGE,"E6.filletArc")])]});
            booleanBodies(context, id + "F5", {"operationType" : BooleanOperationType.SUBTRACTION, "tools" : qUnion([Q0, Q1, Q2, Q3, Q4, Q5, Q6, Q7, Q8, Q9, Q10, Q11]), "targets" : qUnion([Q12])});
        }
        {
            var Q0;
            Q0=makeQuery(id+"F5.opBoolean","SPLIT",FACE,{"disambiguationData":[TD([makeQuery(id+"F3.opExtrude","SWEPT_FACE",FACE,{"disambiguationData":[OSD([sQuery(id+"F2.wireOp",EDGE,"E46")])]})])],"derivedFrom":makeQuery(id+"F1.opExtrude","CAP_FACE",FACE,{"disambiguationData":[OSD([sQuery(id+"F0.wireOp",EDGE,"E0"),sQuery(id+"F0.wireOp",EDGE,"E1"),sQuery(id+"F0.wireOp",EDGE,"E2"),sQuery(id+"F0.wireOp",EDGE,"E3"),sQuery(id+"F0.wireOp",EDGE,"E4"),sQuery(id+"F0.wireOp",EDGE,"E5.filletArc"),sQuery(id+"F0.wireOp",EDGE,"E6.filletArc")])],"isStart":false})});
            var sketch = newSketch(context, id + "F6", { "sketchPlane" : qUnion([Q0])});
            skLineSegment(sketch, "E205.bottom", {"start": v(-27.35, 16.96) * mm, "end": v(-26.55, 16.96) * mm});
            skLineSegment(sketch, "E205.top", {"start": v(-27.35, 0.45) * mm, "end": v(-26.55, 0.45) * mm});
            skLineSegment(sketch, "E205.left", {"start": v(-27.35, 16.96) * mm, "end": v(-27.35, 0.45) * mm});
            skLineSegment(sketch, "E205.right", {"start": v(-26.55, 16.96) * mm, "end": v(-26.55, 0.45) * mm});
            skLineSegment(sketch, "E206.bottom", {"start": v(-9.99, 8.4) * mm, "end": v(-10.79, 8.4) * mm});
            skLineSegment(sketch, "E206.top", {"start": v(-9.99, 5.36) * mm, "end": v(-10.79, 5.36) * mm});
            skLineSegment(sketch, "E206.left", {"start": v(-9.99, 8.4) * mm, "end": v(-9.99, 5.36) * mm});
            skLineSegment(sketch, "E206.right", {"start": v(-10.79, 8.4) * mm, "end": v(-10.79, 5.36) * mm});
            skArc(sketch, "E207", {"start": v(-9.99, 5.31) * mm, "mid": v(-10.02, 3.9) * mm, "end": v(-9.62, 2.55) * mm});
            skArc(sketch, "E208.0", {"start": v(-10.86, 4.7) * mm, "mid": v(-10.74, 3.36) * mm, "end": v(-10.28, 2.08) * mm});
            skLineSegment(sketch, "E209", {"start": v(-9.62, 2.55) * mm, "end": v(-10.28, 2.08) * mm});
            skLineSegment(sketch, "E210", {"start": v(-9.99, 5.31) * mm, "end": v(-10.86, 4.7) * mm});
            skLineSegment(sketch, "E211.bottom", {"start": v(25.14, 7.8) * mm, "end": v(13.74, 7.8) * mm});
            skLineSegment(sketch, "E211.top", {"start": v(25.14, 8.6) * mm, "end": v(13.74, 8.6) * mm});
            skLineSegment(sketch, "E211.left", {"start": v(25.14, 7.8) * mm, "end": v(25.14, 8.6) * mm});
            skLineSegment(sketch, "E211.right", {"start": v(13.74, 7.8) * mm, "end": v(13.74, 8.6) * mm});
            skLineSegment(sketch, "E212", {"start": v(-22.78, -6.45) * mm, "end": v(-14.4, -15.03) * mm});
            skLineSegment(sketch, "E213", {"start": v(-14.4, -15.03) * mm, "end": v(-14.97, -15.6) * mm});
            skLineSegment(sketch, "E214", {"start": v(-14.97, -15.6) * mm, "end": v(-23.36, -7) * mm});
            skLineSegment(sketch, "E215", {"start": v(-23.36, -7) * mm, "end": v(-22.78, -6.45) * mm});
            skLineSegment(sketch, "E216", {"start": v(-19.47, -6.65) * mm, "end": v(-10.1, -16.13) * mm});
            skLineSegment(sketch, "E217", {"start": v(-10.1, -16.13) * mm, "end": v(-9.53, -15.57) * mm});
            skLineSegment(sketch, "E218", {"start": v(-9.53, -15.57) * mm, "end": v(-18.9, -6.09) * mm});
            skLineSegment(sketch, "E219", {"start": v(-18.9, -6.09) * mm, "end": v(-19.47, -6.65) * mm});
            skLineSegment(sketch, "E220.bottom", {"start": v(-5.33, -0.64) * mm, "end": v(-4.53, -0.64) * mm});
            skLineSegment(sketch, "E220.top", {"start": v(-5.33, -17.15) * mm, "end": v(-4.53, -17.15) * mm});
            skLineSegment(sketch, "E220.left", {"start": v(-5.33, -0.64) * mm, "end": v(-5.33, -17.15) * mm});
            skLineSegment(sketch, "E220.right", {"start": v(-4.53, -0.64) * mm, "end": v(-4.53, -17.15) * mm});
            skLineSegment(sketch, "E221.bottom", {"start": v(8.52, -4.32) * mm, "end": v(9.32, -4.32) * mm});
            skLineSegment(sketch, "E221.top", {"start": v(8.52, -17.4) * mm, "end": v(9.32, -17.4) * mm});
            skLineSegment(sketch, "E221.left", {"start": v(8.52, -4.32) * mm, "end": v(8.52, -17.4) * mm});
            skLineSegment(sketch, "E221.right", {"start": v(9.32, -4.32) * mm, "end": v(9.32, -17.4) * mm});
            skSolve(sketch);
        }
        {
            var Q0;
            {var subQ1=sQuery(id+"F6.wireOp",EDGE,"E205.bottom");Q0=makeQuery(id+"F6.imprint","IMPRINT",FACE,{"disambiguationData":[TD([[makeQuery(id+"F6.imprint","IMPRINT",EDGE,{"derivedFrom":subQ1}),-1.0]])]});}
            var Q1;
            {var subQ1=sQuery(id+"F6.wireOp",EDGE,"E205.top");Q1=makeQuery(id+"F6.imprint","IMPRINT",FACE,{"disambiguationData":[TD([[makeQuery(id+"F6.imprint","IMPRINT",EDGE,{"derivedFrom":subQ1}),1.0]])]});}
            var Q2;
            {var subQ4=sQuery(id+"F6.wireOp",EDGE,"E205.left");var subQ17=makeQuery(id+"F6.imprint","IMPRINT",VERTEX,{"derivedFrom":subQ4});Q2=makeQuery(id+"F6.imprint","IMPRINT",FACE,{"disambiguationData":[TD([[makeQuery(id+"F6.imprint","IMPRINT",EDGE,{"disambiguationData":[TD([[subQ17,1.0]])],"derivedFrom":subQ4}),-1.0]])]});}
            var Q3;
            Q3=makeQuery(id+"F6.imprint","IMPRINT",FACE,{"disambiguationData":[TD([[makeQuery(id+"F6.imprint","IMPRINT",EDGE,{"derivedFrom":sQuery(id+"F6.wireOp",EDGE,"E206.bottom")}),1.0]])]});
            var Q4;
            Q4=makeQuery(id+"F6.imprint","IMPRINT",FACE,{"disambiguationData":[TD([[makeQuery(id+"F6.imprint","IMPRINT",EDGE,{"derivedFrom":sQuery(id+"F6.wireOp",EDGE,"E207")}),-1.0]])]});
            var Q5;
            Q5=makeQuery(id+"F6.imprint","IMPRINT",FACE,{"disambiguationData":[TD([[makeQuery(id+"F6.imprint","IMPRINT",EDGE,{"derivedFrom":sQuery(id+"F6.wireOp",EDGE,"E211.bottom")}),-1.0]])]});
            var Q6;
            Q6=makeQuery(id+"F6.imprint","IMPRINT",FACE,{"disambiguationData":[TD([[makeQuery(id+"F6.imprint","IMPRINT",EDGE,{"derivedFrom":sQuery(id+"F6.wireOp",EDGE,"E212")}),-1.0]])]});
            var Q7;
            Q7=makeQuery(id+"F6.imprint","IMPRINT",FACE,{"disambiguationData":[TD([[makeQuery(id+"F6.imprint","IMPRINT",EDGE,{"derivedFrom":sQuery(id+"F6.wireOp",EDGE,"E216")}),1.0]])]});
            var Q8;
            Q8=makeQuery(id+"F6.imprint","IMPRINT",FACE,{"disambiguationData":[TD([[makeQuery(id+"F6.imprint","IMPRINT",EDGE,{"derivedFrom":sQuery(id+"F6.wireOp",EDGE,"E220.bottom")}),-1.0]])]});
            var Q9;
            Q9=makeQuery(id+"F6.imprint","IMPRINT",FACE,{"disambiguationData":[TD([[makeQuery(id+"F6.imprint","IMPRINT",EDGE,{"derivedFrom":sQuery(id+"F6.wireOp",EDGE,"E221.bottom")}),-1.0]])]});
            var Q10;
            {var subQ0=sQuery(id+"F0.wireOp",EDGE,"E1");var subQ1=sQuery(id+"F0.wireOp",EDGE,"E3");var subQ2=sQuery(id+"F0.wireOp",EDGE,"E0");var subQ3=sQuery(id+"F0.wireOp",EDGE,"E4");var subQ4=sQuery(id+"F0.wireOp",EDGE,"E5.filletArc");var subQ5=sQuery(id+"F0.wireOp",EDGE,"E6.filletArc");var subQ6=sQuery(id+"F0.wireOp",EDGE,"E2");Q10=makeQuery(id+"F5.opBoolean","SPLIT",FACE,{"disambiguationData":[TD([makeQuery(id+"F1.opExtrude","SWEPT_FACE",FACE,{"disambiguationData":[OSD([subQ2])]})])],"derivedFrom":makeQuery(id+"F1.opExtrude","CAP_FACE",FACE,{"disambiguationData":[OSD([subQ2,subQ0,subQ6,subQ1,subQ3,subQ4,subQ5])],"isStart":true})});}
            extrude(context, id + "F7", {"entities" : qUnion([Q0, Q1, Q2, Q3, Q4, Q5, Q6, Q7, Q8, Q9]), "operationType" : NewBodyOperationType.ADD, "endBound" : BoundingType.UP_TO_SURFACE, "oppositeDirection" : true, "depth" : 25 * mm, "endBoundEntityFace" : qUnion([Q10]), "offsetDistance" : 25 * mm});
        }
    });
